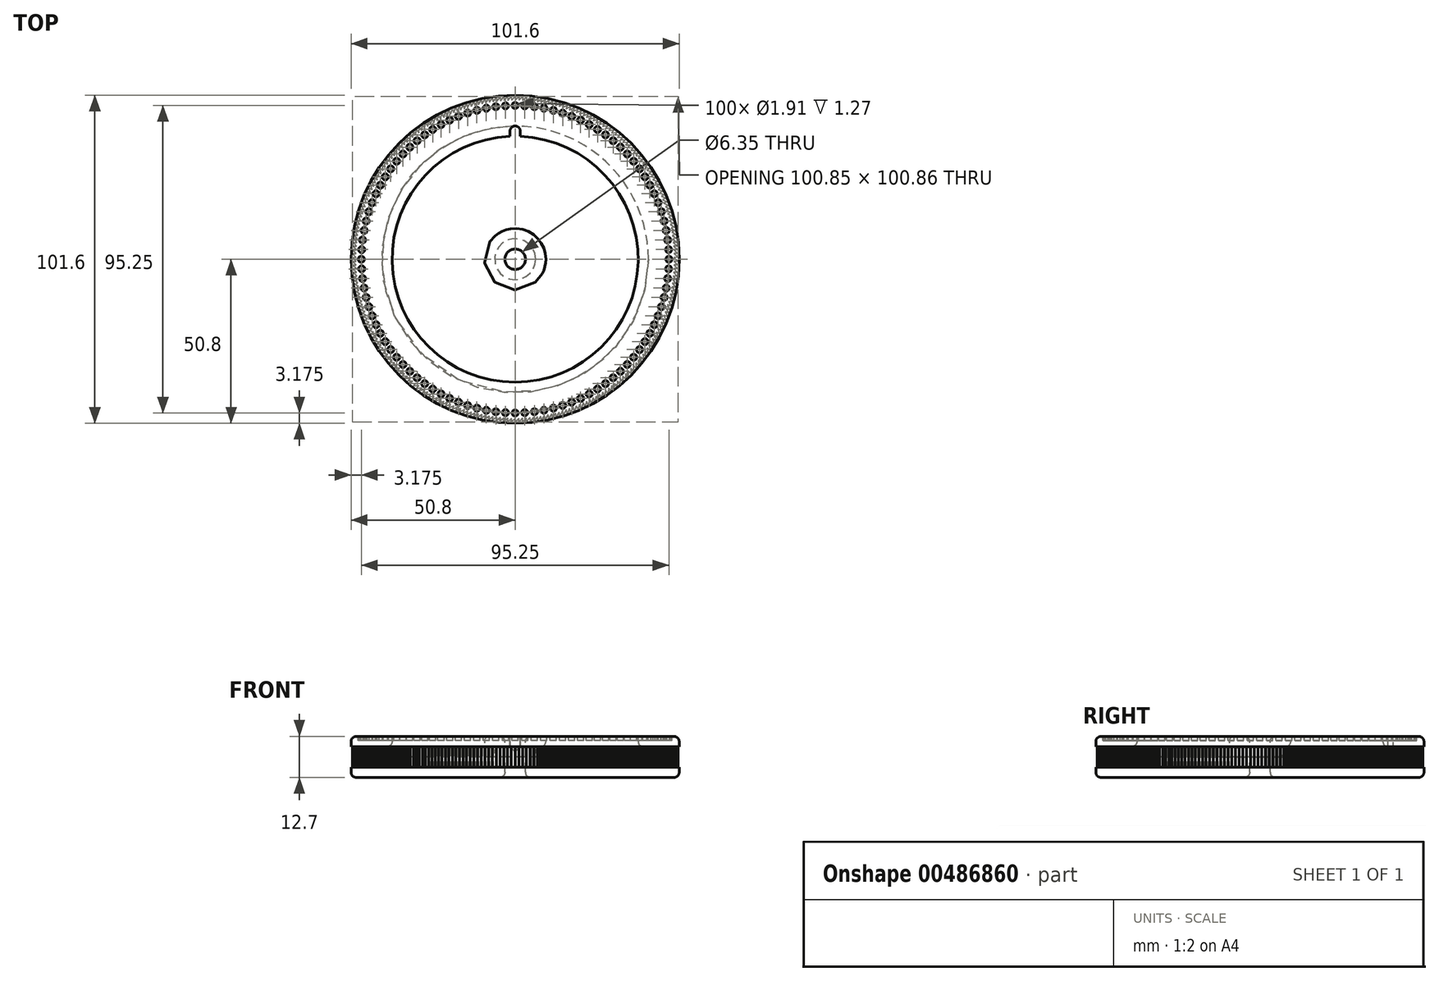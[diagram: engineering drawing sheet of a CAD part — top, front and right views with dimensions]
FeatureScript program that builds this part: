
annotation { "Feature Type Name" : "Feature", "Feature Type Description" : "" }
export const myFeature = defineFeature(function(context is Context, id is Id, definition is map)
    precondition{}
    {
        {
            var Q0;
            Q0=qCreatedBy(makeId("Top.planeOp"),FACE);
            var sketch = newSketch(context, id + "F0", { "sketchPlane" : qUnion([Q0])});
            skCircle(sketch, "E0", {"center": v(0, 0) * mm, "radius": 50.8 * mm});
            skSolve(sketch);
        }
        {
            var Q0;
            Q0 = qSketchRegion(id + "F0", true);
            extrude(context, id + "F1", {"entities" : qUnion([Q0]), "depth" : 12.7 * mm});
        }
        {
            var Q0;
            Q0=makeQuery(id+"F1.opExtrude","CAP_FACE",FACE,{"disambiguationData":[OSD([sQuery(id+"F0.wireOp",EDGE,"E0")])],"isStart":false});
            var sketch = newSketch(context, id + "F2", { "sketchPlane" : qUnion([Q0])});
            skCircle(sketch, "E1", {"center": v(0, 0) * mm, "radius": 38.1 * mm});
            skLineSegment(sketch, "E2", {"start": v(0, 0) * mm, "end": v(-3.18, 37.97) * mm});
            skLineSegment(sketch, "E3", {"start": v(0, 0) * mm, "end": v(0, 38.1) * mm});
            skLineSegment(sketch, "E4.1.0", {"start": v(0, 0) * mm, "end": v(-29.1, 24.6) * mm});
            skLineSegment(sketch, "E4.1.1", {"start": v(0, 0) * mm, "end": v(-26.94, 26.94) * mm});
            skLineSegment(sketch, "E4.2.0", {"start": v(0, 0) * mm, "end": v(-37.97, -3.17) * mm});
            skLineSegment(sketch, "E4.2.1", {"start": v(0, 0) * mm, "end": v(-38.1, 0) * mm});
            skLineSegment(sketch, "E4.3.0", {"start": v(0, 0) * mm, "end": v(-24.6, -29.1) * mm});
            skLineSegment(sketch, "E4.3.1", {"start": v(0, 0) * mm, "end": v(-26.94, -26.94) * mm});
            skLineSegment(sketch, "E4.4.0", {"start": v(0, 0) * mm, "end": v(3.17, -37.97) * mm});
            skLineSegment(sketch, "E4.4.1", {"start": v(0, 0) * mm, "end": v(0, -38.1) * mm});
            skLineSegment(sketch, "E4.5.0", {"start": v(0, 0) * mm, "end": v(29.1, -24.6) * mm});
            skLineSegment(sketch, "E4.5.1", {"start": v(0, 0) * mm, "end": v(26.94, -26.94) * mm});
            skLineSegment(sketch, "E4.6.0", {"start": v(0, 0) * mm, "end": v(37.97, 3.17) * mm});
            skLineSegment(sketch, "E4.6.1", {"start": v(0, 0) * mm, "end": v(38.1, 0) * mm});
            skLineSegment(sketch, "E4.7.0", {"start": v(0, 0) * mm, "end": v(24.6, 29.1) * mm});
            skLineSegment(sketch, "E4.7.1", {"start": v(0, 0) * mm, "end": v(26.94, 26.94) * mm});
            skCircle(sketch, "E5", {"center": v(0, 0) * mm, "radius": 3.18 * mm});
            skSolve(sketch);
        }
        {
            var Q0;
            Q0 = qSketchRegion(id + "F2", true);
            var Q1;
            {var subQ1=sQuery(id+"F2.wireOp",EDGE,"E3");var subQ3=sQuery(id+"F2.wireOp",EDGE,"E5");var subQ4=makeQuery(id+"F2.imprint","INTERSECT",VERTEX,{"derivedFrom":[subQ1,subQ3]});Q1=makeQuery(id+"F2.imprint","IMPRINT",FACE,{"disambiguationData":[TD([[makeQuery(id+"F2.imprint","IMPRINT",EDGE,{"disambiguationData":[TD([[subQ4,1.0]])],"derivedFrom":subQ3}),1.0]])]});}
            var Q2;
            {var subQ1=sQuery(id+"F2.wireOp",EDGE,"E4.6.0");var subQ3=sQuery(id+"F2.wireOp",EDGE,"E5");var subQ4=makeQuery(id+"F2.imprint","INTERSECT",VERTEX,{"derivedFrom":[subQ1,subQ3]});Q2=makeQuery(id+"F2.imprint","IMPRINT",FACE,{"disambiguationData":[TD([[makeQuery(id+"F2.imprint","IMPRINT",EDGE,{"disambiguationData":[TD([[subQ4,-1.0]])],"derivedFrom":subQ3}),1.0]])]});}
            var Q3;
            {var subQ1=sQuery(id+"F2.wireOp",EDGE,"E4.2.0");var subQ3=sQuery(id+"F2.wireOp",EDGE,"E5");var subQ4=makeQuery(id+"F2.imprint","INTERSECT",VERTEX,{"derivedFrom":[subQ1,subQ3]});Q3=makeQuery(id+"F2.imprint","IMPRINT",FACE,{"disambiguationData":[TD([[makeQuery(id+"F2.imprint","IMPRINT",EDGE,{"disambiguationData":[TD([[subQ4,-1.0]])],"derivedFrom":subQ3}),1.0]])]});}
            var Q4;
            {var subQ1=sQuery(id+"F2.wireOp",EDGE,"E4.1.0");var subQ3=sQuery(id+"F2.wireOp",EDGE,"E5");var subQ4=makeQuery(id+"F2.imprint","INTERSECT",VERTEX,{"derivedFrom":[subQ1,subQ3]});Q4=makeQuery(id+"F2.imprint","IMPRINT",FACE,{"disambiguationData":[TD([[makeQuery(id+"F2.imprint","IMPRINT",EDGE,{"disambiguationData":[TD([[subQ4,-1.0]])],"derivedFrom":subQ3}),1.0]])]});}
            var Q5;
            {var subQ1=sQuery(id+"F2.wireOp",EDGE,"E4.3.0");var subQ3=sQuery(id+"F2.wireOp",EDGE,"E5");var subQ4=makeQuery(id+"F2.imprint","INTERSECT",VERTEX,{"derivedFrom":[subQ1,subQ3]});Q5=makeQuery(id+"F2.imprint","IMPRINT",FACE,{"disambiguationData":[TD([[makeQuery(id+"F2.imprint","IMPRINT",EDGE,{"disambiguationData":[TD([[subQ4,-1.0]])],"derivedFrom":subQ3}),1.0]])]});}
            var Q6;
            {var subQ1=sQuery(id+"F2.wireOp",EDGE,"E4.4.0");var subQ3=sQuery(id+"F2.wireOp",EDGE,"E5");var subQ4=makeQuery(id+"F2.imprint","INTERSECT",VERTEX,{"derivedFrom":[subQ1,subQ3]});Q6=makeQuery(id+"F2.imprint","IMPRINT",FACE,{"disambiguationData":[TD([[makeQuery(id+"F2.imprint","IMPRINT",EDGE,{"disambiguationData":[TD([[subQ4,-1.0]])],"derivedFrom":subQ3}),1.0]])]});}
            var Q7;
            {var subQ1=sQuery(id+"F2.wireOp",EDGE,"E4.5.0");var subQ3=sQuery(id+"F2.wireOp",EDGE,"E5");var subQ4=makeQuery(id+"F2.imprint","INTERSECT",VERTEX,{"derivedFrom":[subQ1,subQ3]});Q7=makeQuery(id+"F2.imprint","IMPRINT",FACE,{"disambiguationData":[TD([[makeQuery(id+"F2.imprint","IMPRINT",EDGE,{"disambiguationData":[TD([[subQ4,-1.0]])],"derivedFrom":subQ3}),1.0]])]});}
            var Q8;
            {var subQ1=sQuery(id+"F2.wireOp",EDGE,"E2");var subQ3=sQuery(id+"F2.wireOp",EDGE,"E5");var subQ4=makeQuery(id+"F2.imprint","INTERSECT",VERTEX,{"derivedFrom":[subQ1,subQ3]});Q8=makeQuery(id+"F2.imprint","IMPRINT",FACE,{"disambiguationData":[TD([[makeQuery(id+"F2.imprint","IMPRINT",EDGE,{"disambiguationData":[TD([[subQ4,1.0]])],"derivedFrom":subQ3}),1.0]])]});}
            var Q9;
            {var subQ1=sQuery(id+"F2.wireOp",EDGE,"E2");var subQ3=sQuery(id+"F2.wireOp",EDGE,"E5");var subQ4=makeQuery(id+"F2.imprint","INTERSECT",VERTEX,{"derivedFrom":[subQ1,subQ3]});Q9=makeQuery(id+"F2.imprint","IMPRINT",FACE,{"disambiguationData":[TD([[makeQuery(id+"F2.imprint","IMPRINT",EDGE,{"disambiguationData":[TD([[subQ4,-1.0]])],"derivedFrom":subQ3}),1.0]])]});}
            var Q10;
            {var subQ1=sQuery(id+"F2.wireOp",EDGE,"E4.1.0");var subQ3=sQuery(id+"F2.wireOp",EDGE,"E5");var subQ4=makeQuery(id+"F2.imprint","INTERSECT",VERTEX,{"derivedFrom":[subQ1,subQ3]});Q10=makeQuery(id+"F2.imprint","IMPRINT",FACE,{"disambiguationData":[TD([[makeQuery(id+"F2.imprint","IMPRINT",EDGE,{"disambiguationData":[TD([[subQ4,1.0]])],"derivedFrom":subQ3}),1.0]])]});}
            var Q11;
            {var subQ1=sQuery(id+"F2.wireOp",EDGE,"E4.2.0");var subQ3=sQuery(id+"F2.wireOp",EDGE,"E5");var subQ4=makeQuery(id+"F2.imprint","INTERSECT",VERTEX,{"derivedFrom":[subQ1,subQ3]});Q11=makeQuery(id+"F2.imprint","IMPRINT",FACE,{"disambiguationData":[TD([[makeQuery(id+"F2.imprint","IMPRINT",EDGE,{"disambiguationData":[TD([[subQ4,1.0]])],"derivedFrom":subQ3}),1.0]])]});}
            var Q12;
            {var subQ1=sQuery(id+"F2.wireOp",EDGE,"E4.7.0");var subQ3=sQuery(id+"F2.wireOp",EDGE,"E5");var subQ4=makeQuery(id+"F2.imprint","INTERSECT",VERTEX,{"derivedFrom":[subQ1,subQ3]});Q12=makeQuery(id+"F2.imprint","IMPRINT",FACE,{"disambiguationData":[TD([[makeQuery(id+"F2.imprint","IMPRINT",EDGE,{"disambiguationData":[TD([[subQ4,1.0]])],"derivedFrom":subQ3}),1.0]])]});}
            var Q13;
            {var subQ1=sQuery(id+"F2.wireOp",EDGE,"E4.3.0");var subQ3=sQuery(id+"F2.wireOp",EDGE,"E5");var subQ4=makeQuery(id+"F2.imprint","INTERSECT",VERTEX,{"derivedFrom":[subQ1,subQ3]});Q13=makeQuery(id+"F2.imprint","IMPRINT",FACE,{"disambiguationData":[TD([[makeQuery(id+"F2.imprint","IMPRINT",EDGE,{"disambiguationData":[TD([[subQ4,1.0]])],"derivedFrom":subQ3}),1.0]])]});}
            var Q14;
            {var subQ1=sQuery(id+"F2.wireOp",EDGE,"E4.4.0");var subQ3=sQuery(id+"F2.wireOp",EDGE,"E5");var subQ4=makeQuery(id+"F2.imprint","INTERSECT",VERTEX,{"derivedFrom":[subQ1,subQ3]});Q14=makeQuery(id+"F2.imprint","IMPRINT",FACE,{"disambiguationData":[TD([[makeQuery(id+"F2.imprint","IMPRINT",EDGE,{"disambiguationData":[TD([[subQ4,1.0]])],"derivedFrom":subQ3}),1.0]])]});}
            var Q15;
            {var subQ1=sQuery(id+"F2.wireOp",EDGE,"E4.5.0");var subQ3=sQuery(id+"F2.wireOp",EDGE,"E5");var subQ4=makeQuery(id+"F2.imprint","INTERSECT",VERTEX,{"derivedFrom":[subQ1,subQ3]});Q15=makeQuery(id+"F2.imprint","IMPRINT",FACE,{"disambiguationData":[TD([[makeQuery(id+"F2.imprint","IMPRINT",EDGE,{"disambiguationData":[TD([[subQ4,1.0]])],"derivedFrom":subQ3}),1.0]])]});}
            var Q16;
            {var subQ1=sQuery(id+"F2.wireOp",EDGE,"E4.6.0");var subQ3=sQuery(id+"F2.wireOp",EDGE,"E5");var subQ4=makeQuery(id+"F2.imprint","INTERSECT",VERTEX,{"derivedFrom":[subQ1,subQ3]});Q16=makeQuery(id+"F2.imprint","IMPRINT",FACE,{"disambiguationData":[TD([[makeQuery(id+"F2.imprint","IMPRINT",EDGE,{"disambiguationData":[TD([[subQ4,1.0]])],"derivedFrom":subQ3}),1.0]])]});}
            extrude(context, id + "F3", {"entities" : qUnion([Q0, Q1, Q2, Q3, Q4, Q5, Q6, Q7, Q8, Q9, Q10, Q11, Q12, Q13, Q14, Q15, Q16]), "operationType" : NewBodyOperationType.REMOVE, "oppositeDirection" : true, "depth" : 6.35 * mm});
        }
        {
            var Q0;
            Q0=makeQuery(id+"F3.boolean.opBoolean","COPY",FACE,{"derivedFrom":makeQuery(id+"F3.opExtrude","CAP_FACE",FACE,{"disambiguationData":[OSD([sQuery(id+"F2.wireOp",EDGE,"E1")])],"isStart":false})});
            var sketch = newSketch(context, id + "F4", { "sketchPlane" : qUnion([Q0])});
            skCircle(sketch, "E6", {"center": v(0, 0) * mm, "radius": 3.18 * mm});
            skSolve(sketch);
        }
        {
            var Q0;
            Q0 = qSketchRegion(id + "F4", true);
            extrude(context, id + "F5", {"entities" : qUnion([Q0]), "operationType" : NewBodyOperationType.REMOVE, "oppositeDirection" : true, "depth" : 25.4 * mm});
        }
        {
            var Q0;
            Q0=qCreatedBy(makeId("Top.planeOp"),FACE);
            var sketch = newSketch(context, id + "F6", { "sketchPlane" : qUnion([Q0])});
            skLineSegment(sketch, "E7", {"start": v(0, 51.65) * mm, "end": v(0, 49.24) * mm});
            skLineSegment(sketch, "E8", {"start": v(0, 49.24) * mm, "end": v(2.41, 51.65) * mm});
            skLineSegment(sketch, "E9", {"start": v(2.41, 51.65) * mm, "end": v(0, 51.65) * mm});
            skLineSegment(sketch, "E10.1.0", {"start": v(-1.2, 51.64) * mm, "end": v(-1.15, 49.23) * mm});
            skLineSegment(sketch, "E10.1.1", {"start": v(1.2, 51.7) * mm, "end": v(-1.2, 51.64) * mm});
            skLineSegment(sketch, "E10.1.2", {"start": v(-1.15, 49.23) * mm, "end": v(1.2, 51.7) * mm});
            skLineSegment(sketch, "E10.2.0", {"start": v(-2.4, 51.6) * mm, "end": v(-2.3, 49.19) * mm});
            skLineSegment(sketch, "E10.2.1", {"start": v(0, 51.7) * mm, "end": v(-2.4, 51.6) * mm});
            skLineSegment(sketch, "E10.2.2", {"start": v(-2.3, 49.19) * mm, "end": v(0, 51.7) * mm});
            skLineSegment(sketch, "E10.3.0", {"start": v(-3.6, 51.53) * mm, "end": v(-3.43, 49.12) * mm});
            skLineSegment(sketch, "E10.3.1", {"start": v(-1.2, 51.7) * mm, "end": v(-3.6, 51.53) * mm});
            skLineSegment(sketch, "E10.3.2", {"start": v(-3.43, 49.12) * mm, "end": v(-1.2, 51.7) * mm});
            skLineSegment(sketch, "E10.4.0", {"start": v(-4.8, 51.43) * mm, "end": v(-4.58, 49.03) * mm});
            skLineSegment(sketch, "E10.4.1", {"start": v(-2.4, 51.65) * mm, "end": v(-4.8, 51.43) * mm});
            skLineSegment(sketch, "E10.4.2", {"start": v(-4.58, 49.03) * mm, "end": v(-2.4, 51.65) * mm});
            skLineSegment(sketch, "E10.5.0", {"start": v(-6, 51.3) * mm, "end": v(-5.72, 48.9) * mm});
            skLineSegment(sketch, "E10.5.1", {"start": v(-3.6, 51.58) * mm, "end": v(-6, 51.3) * mm});
            skLineSegment(sketch, "E10.5.2", {"start": v(-5.72, 48.9) * mm, "end": v(-3.6, 51.58) * mm});
            skLineSegment(sketch, "E10.6.0", {"start": v(-7.19, 51.15) * mm, "end": v(-6.85, 48.76) * mm});
            skLineSegment(sketch, "E10.6.1", {"start": v(-4.8, 51.49) * mm, "end": v(-7.19, 51.15) * mm});
            skLineSegment(sketch, "E10.6.2", {"start": v(-6.85, 48.76) * mm, "end": v(-4.8, 51.49) * mm});
            skLineSegment(sketch, "E10.7.0", {"start": v(-8.38, 50.97) * mm, "end": v(-7.99, 48.59) * mm});
            skLineSegment(sketch, "E10.7.1", {"start": v(-6, 51.36) * mm, "end": v(-8.38, 50.97) * mm});
            skLineSegment(sketch, "E10.7.2", {"start": v(-7.99, 48.59) * mm, "end": v(-6, 51.36) * mm});
            skLineSegment(sketch, "E10.8.0", {"start": v(-9.56, 50.76) * mm, "end": v(-9.11, 48.39) * mm});
            skLineSegment(sketch, "E10.8.1", {"start": v(-7.19, 51.2) * mm, "end": v(-9.56, 50.76) * mm});
            skLineSegment(sketch, "E10.8.2", {"start": v(-9.11, 48.39) * mm, "end": v(-7.19, 51.2) * mm});
            skLineSegment(sketch, "E10.9.0", {"start": v(-10.74, 50.52) * mm, "end": v(-10.24, 48.16) * mm});
            skLineSegment(sketch, "E10.9.1", {"start": v(-8.38, 51.03) * mm, "end": v(-10.74, 50.52) * mm});
            skLineSegment(sketch, "E10.9.2", {"start": v(-10.24, 48.16) * mm, "end": v(-8.38, 51.03) * mm});
            skLineSegment(sketch, "E10.10.0", {"start": v(-11.91, 50.26) * mm, "end": v(-11.36, 47.91) * mm});
            skLineSegment(sketch, "E10.10.1", {"start": v(-9.56, 50.82) * mm, "end": v(-11.91, 50.26) * mm});
            skLineSegment(sketch, "E10.10.2", {"start": v(-11.36, 47.91) * mm, "end": v(-9.56, 50.82) * mm});
            skLineSegment(sketch, "E10.11.0", {"start": v(-13.08, 49.97) * mm, "end": v(-12.47, 47.64) * mm});
            skLineSegment(sketch, "E10.11.1", {"start": v(-10.74, 50.58) * mm, "end": v(-13.08, 49.97) * mm});
            skLineSegment(sketch, "E10.11.2", {"start": v(-12.47, 47.64) * mm, "end": v(-10.74, 50.58) * mm});
            skLineSegment(sketch, "E10.12.0", {"start": v(-14.24, 49.65) * mm, "end": v(-13.57, 47.33) * mm});
            skLineSegment(sketch, "E10.12.1", {"start": v(-11.92, 50.32) * mm, "end": v(-14.24, 49.65) * mm});
            skLineSegment(sketch, "E10.12.2", {"start": v(-13.57, 47.33) * mm, "end": v(-11.92, 50.32) * mm});
            skLineSegment(sketch, "E10.13.0", {"start": v(-15.39, 49.3) * mm, "end": v(-14.67, 47) * mm});
            skLineSegment(sketch, "E10.13.1", {"start": v(-13.09, 50.03) * mm, "end": v(-15.39, 49.3) * mm});
            skLineSegment(sketch, "E10.13.2", {"start": v(-14.67, 47) * mm, "end": v(-13.09, 50.03) * mm});
            skLineSegment(sketch, "E10.14.0", {"start": v(-16.53, 48.94) * mm, "end": v(-15.76, 46.65) * mm});
            skLineSegment(sketch, "E10.14.1", {"start": v(-14.25, 49.7) * mm, "end": v(-16.53, 48.94) * mm});
            skLineSegment(sketch, "E10.14.2", {"start": v(-15.76, 46.65) * mm, "end": v(-14.25, 49.7) * mm});
            skLineSegment(sketch, "E10.15.0", {"start": v(-17.67, 48.54) * mm, "end": v(-16.84, 46.27) * mm});
            skLineSegment(sketch, "E10.15.1", {"start": v(-15.4, 49.36) * mm, "end": v(-17.67, 48.54) * mm});
            skLineSegment(sketch, "E10.15.2", {"start": v(-16.84, 46.27) * mm, "end": v(-15.4, 49.36) * mm});
            skLineSegment(sketch, "E10.16.0", {"start": v(-18.8, 48.11) * mm, "end": v(-17.91, 45.87) * mm});
            skLineSegment(sketch, "E10.16.1", {"start": v(-16.54, 49) * mm, "end": v(-18.8, 48.11) * mm});
            skLineSegment(sketch, "E10.16.2", {"start": v(-17.91, 45.87) * mm, "end": v(-16.54, 49) * mm});
            skLineSegment(sketch, "E10.17.0", {"start": v(-19.9, 47.66) * mm, "end": v(-18.98, 45.44) * mm});
            skLineSegment(sketch, "E10.17.1", {"start": v(-17.68, 48.6) * mm, "end": v(-19.9, 47.66) * mm});
            skLineSegment(sketch, "E10.17.2", {"start": v(-18.98, 45.44) * mm, "end": v(-17.68, 48.6) * mm});
            skLineSegment(sketch, "E10.18.0", {"start": v(-21, 47.19) * mm, "end": v(-20.03, 44.98) * mm});
            skLineSegment(sketch, "E10.18.1", {"start": v(-18.8, 48.17) * mm, "end": v(-21, 47.19) * mm});
            skLineSegment(sketch, "E10.18.2", {"start": v(-20.03, 44.98) * mm, "end": v(-18.8, 48.17) * mm});
            skLineSegment(sketch, "E10.19.0", {"start": v(-22.1, 46.69) * mm, "end": v(-21.07, 44.5) * mm});
            skLineSegment(sketch, "E10.19.1", {"start": v(-19.92, 47.72) * mm, "end": v(-22.1, 46.69) * mm});
            skLineSegment(sketch, "E10.19.2", {"start": v(-21.07, 44.5) * mm, "end": v(-19.92, 47.72) * mm});
            skLineSegment(sketch, "E10.20.0", {"start": v(-23.18, 46.16) * mm, "end": v(-22.1, 44) * mm});
            skLineSegment(sketch, "E10.20.1", {"start": v(-21.03, 47.24) * mm, "end": v(-23.18, 46.16) * mm});
            skLineSegment(sketch, "E10.20.2", {"start": v(-22.1, 44) * mm, "end": v(-21.03, 47.24) * mm});
            skLineSegment(sketch, "E10.21.0", {"start": v(-24.25, 45.6) * mm, "end": v(-23.12, 43.48) * mm});
            skLineSegment(sketch, "E10.21.1", {"start": v(-22.12, 46.74) * mm, "end": v(-24.25, 45.6) * mm});
            skLineSegment(sketch, "E10.21.2", {"start": v(-23.12, 43.48) * mm, "end": v(-22.12, 46.74) * mm});
            skLineSegment(sketch, "E10.22.0", {"start": v(-25.3, 45.03) * mm, "end": v(-24.12, 42.93) * mm});
            skLineSegment(sketch, "E10.22.1", {"start": v(-23.2, 46.21) * mm, "end": v(-25.3, 45.03) * mm});
            skLineSegment(sketch, "E10.22.2", {"start": v(-24.12, 42.93) * mm, "end": v(-23.2, 46.21) * mm});
            skLineSegment(sketch, "E10.23.0", {"start": v(-26.35, 44.43) * mm, "end": v(-25.11, 42.35) * mm});
            skLineSegment(sketch, "E10.23.1", {"start": v(-24.27, 45.66) * mm, "end": v(-26.35, 44.43) * mm});
            skLineSegment(sketch, "E10.23.2", {"start": v(-25.11, 42.35) * mm, "end": v(-24.27, 45.66) * mm});
            skLineSegment(sketch, "E10.24.0", {"start": v(-27.37, 43.8) * mm, "end": v(-26.1, 41.76) * mm});
            skLineSegment(sketch, "E10.24.1", {"start": v(-25.33, 45.08) * mm, "end": v(-27.37, 43.8) * mm});
            skLineSegment(sketch, "E10.24.2", {"start": v(-26.1, 41.76) * mm, "end": v(-25.33, 45.08) * mm});
            skLineSegment(sketch, "E10.25.0", {"start": v(-28.38, 43.16) * mm, "end": v(-27.06, 41.14) * mm});
            skLineSegment(sketch, "E10.25.1", {"start": v(-26.37, 44.48) * mm, "end": v(-28.38, 43.16) * mm});
            skLineSegment(sketch, "E10.25.2", {"start": v(-27.06, 41.14) * mm, "end": v(-26.37, 44.48) * mm});
            skLineSegment(sketch, "E10.26.0", {"start": v(-29.38, 42.48) * mm, "end": v(-28, 40.5) * mm});
            skLineSegment(sketch, "E10.26.1", {"start": v(-27.4, 43.86) * mm, "end": v(-29.38, 42.48) * mm});
            skLineSegment(sketch, "E10.26.2", {"start": v(-28, 40.5) * mm, "end": v(-27.4, 43.86) * mm});
            skLineSegment(sketch, "E10.27.0", {"start": v(-30.36, 41.79) * mm, "end": v(-28.94, 39.84) * mm});
            skLineSegment(sketch, "E10.27.1", {"start": v(-28.4, 43.2) * mm, "end": v(-30.36, 41.79) * mm});
            skLineSegment(sketch, "E10.27.2", {"start": v(-28.94, 39.84) * mm, "end": v(-28.4, 43.2) * mm});
            skLineSegment(sketch, "E10.28.0", {"start": v(-31.33, 41.07) * mm, "end": v(-29.86, 39.15) * mm});
            skLineSegment(sketch, "E10.28.1", {"start": v(-29.4, 42.53) * mm, "end": v(-31.33, 41.07) * mm});
            skLineSegment(sketch, "E10.28.2", {"start": v(-29.86, 39.15) * mm, "end": v(-29.4, 42.53) * mm});
            skLineSegment(sketch, "E10.29.0", {"start": v(-32.27, 40.33) * mm, "end": v(-30.77, 38.45) * mm});
            skLineSegment(sketch, "E10.29.1", {"start": v(-30.39, 41.84) * mm, "end": v(-32.27, 40.33) * mm});
            skLineSegment(sketch, "E10.29.2", {"start": v(-30.77, 38.45) * mm, "end": v(-30.39, 41.84) * mm});
            skLineSegment(sketch, "E10.30.0", {"start": v(-33.2, 39.57) * mm, "end": v(-31.65, 37.72) * mm});
            skLineSegment(sketch, "E10.30.1", {"start": v(-31.35, 41.12) * mm, "end": v(-33.2, 39.57) * mm});
            skLineSegment(sketch, "E10.30.2", {"start": v(-31.65, 37.72) * mm, "end": v(-31.35, 41.12) * mm});
            skLineSegment(sketch, "E10.31.0", {"start": v(-34.11, 38.79) * mm, "end": v(-32.52, 36.97) * mm});
            skLineSegment(sketch, "E10.31.1", {"start": v(-32.3, 40.38) * mm, "end": v(-34.11, 38.79) * mm});
            skLineSegment(sketch, "E10.31.2", {"start": v(-32.52, 36.97) * mm, "end": v(-32.3, 40.38) * mm});
            skLineSegment(sketch, "E10.32.0", {"start": v(-35, 37.98) * mm, "end": v(-33.37, 36.2) * mm});
            skLineSegment(sketch, "E10.32.1", {"start": v(-33.23, 39.62) * mm, "end": v(-35, 37.98) * mm});
            skLineSegment(sketch, "E10.32.2", {"start": v(-33.37, 36.2) * mm, "end": v(-33.23, 39.62) * mm});
            skLineSegment(sketch, "E10.33.0", {"start": v(-35.88, 37.16) * mm, "end": v(-34.2, 35.42) * mm});
            skLineSegment(sketch, "E10.33.1", {"start": v(-34.15, 38.83) * mm, "end": v(-35.88, 37.16) * mm});
            skLineSegment(sketch, "E10.33.2", {"start": v(-34.2, 35.42) * mm, "end": v(-34.15, 38.83) * mm});
            skLineSegment(sketch, "E10.34.0", {"start": v(-36.74, 36.31) * mm, "end": v(-35.02, 34.62) * mm});
            skLineSegment(sketch, "E10.34.1", {"start": v(-35.04, 38.03) * mm, "end": v(-36.74, 36.31) * mm});
            skLineSegment(sketch, "E10.34.2", {"start": v(-35.02, 34.62) * mm, "end": v(-35.04, 38.03) * mm});
            skLineSegment(sketch, "E10.35.0", {"start": v(-37.57, 35.45) * mm, "end": v(-35.82, 33.8) * mm});
            skLineSegment(sketch, "E10.35.1", {"start": v(-35.92, 37.2) * mm, "end": v(-37.57, 35.45) * mm});
            skLineSegment(sketch, "E10.35.2", {"start": v(-35.82, 33.8) * mm, "end": v(-35.92, 37.2) * mm});
            skLineSegment(sketch, "E10.36.0", {"start": v(-38.39, 34.56) * mm, "end": v(-36.6, 32.95) * mm});
            skLineSegment(sketch, "E10.36.1", {"start": v(-36.77, 36.36) * mm, "end": v(-38.39, 34.56) * mm});
            skLineSegment(sketch, "E10.36.2", {"start": v(-36.6, 32.95) * mm, "end": v(-36.77, 36.36) * mm});
            skLineSegment(sketch, "E10.37.0", {"start": v(-39.18, 33.66) * mm, "end": v(-37.35, 32.09) * mm});
            skLineSegment(sketch, "E10.37.1", {"start": v(-37.6, 35.5) * mm, "end": v(-39.18, 33.66) * mm});
            skLineSegment(sketch, "E10.37.2", {"start": v(-37.35, 32.09) * mm, "end": v(-37.6, 35.5) * mm});
            skLineSegment(sketch, "E10.38.0", {"start": v(-39.95, 32.74) * mm, "end": v(-38.09, 31.21) * mm});
            skLineSegment(sketch, "E10.38.1", {"start": v(-38.42, 34.6) * mm, "end": v(-39.95, 32.74) * mm});
            skLineSegment(sketch, "E10.38.2", {"start": v(-38.09, 31.21) * mm, "end": v(-38.42, 34.6) * mm});
            skLineSegment(sketch, "E10.39.0", {"start": v(-40.7, 31.8) * mm, "end": v(-38.8, 30.32) * mm});
            skLineSegment(sketch, "E10.39.1", {"start": v(-39.22, 33.7) * mm, "end": v(-40.7, 31.8) * mm});
            skLineSegment(sketch, "E10.39.2", {"start": v(-38.8, 30.32) * mm, "end": v(-39.22, 33.7) * mm});
            skLineSegment(sketch, "E10.40.0", {"start": v(-41.43, 30.85) * mm, "end": v(-39.5, 29.4) * mm});
            skLineSegment(sketch, "E10.40.1", {"start": v(-40, 32.78) * mm, "end": v(-41.43, 30.85) * mm});
            skLineSegment(sketch, "E10.40.2", {"start": v(-39.5, 29.4) * mm, "end": v(-40, 32.78) * mm});
            skLineSegment(sketch, "E10.41.0", {"start": v(-42.14, 29.87) * mm, "end": v(-40.17, 28.48) * mm});
            skLineSegment(sketch, "E10.41.1", {"start": v(-40.74, 31.84) * mm, "end": v(-42.14, 29.87) * mm});
            skLineSegment(sketch, "E10.41.2", {"start": v(-40.17, 28.48) * mm, "end": v(-40.74, 31.84) * mm});
            skLineSegment(sketch, "E10.42.0", {"start": v(-42.82, 28.88) * mm, "end": v(-40.82, 27.54) * mm});
            skLineSegment(sketch, "E10.42.1", {"start": v(-41.47, 30.88) * mm, "end": v(-42.82, 28.88) * mm});
            skLineSegment(sketch, "E10.42.2", {"start": v(-40.82, 27.54) * mm, "end": v(-41.47, 30.88) * mm});
            skLineSegment(sketch, "E10.43.0", {"start": v(-43.48, 27.88) * mm, "end": v(-41.45, 26.58) * mm});
            skLineSegment(sketch, "E10.43.1", {"start": v(-42.18, 29.91) * mm, "end": v(-43.48, 27.88) * mm});
            skLineSegment(sketch, "E10.43.2", {"start": v(-41.45, 26.58) * mm, "end": v(-42.18, 29.91) * mm});
            skLineSegment(sketch, "E10.44.0", {"start": v(-44.12, 26.86) * mm, "end": v(-42.06, 25.6) * mm});
            skLineSegment(sketch, "E10.44.1", {"start": v(-42.87, 28.92) * mm, "end": v(-44.12, 26.86) * mm});
            skLineSegment(sketch, "E10.44.2", {"start": v(-42.06, 25.6) * mm, "end": v(-42.87, 28.92) * mm});
            skLineSegment(sketch, "E10.45.0", {"start": v(-44.73, 25.83) * mm, "end": v(-42.64, 24.62) * mm});
            skLineSegment(sketch, "E10.45.1", {"start": v(-43.53, 27.92) * mm, "end": v(-44.73, 25.83) * mm});
            skLineSegment(sketch, "E10.45.2", {"start": v(-42.64, 24.62) * mm, "end": v(-43.53, 27.92) * mm});
            skLineSegment(sketch, "E10.46.0", {"start": v(-45.32, 24.78) * mm, "end": v(-43.2, 23.62) * mm});
            skLineSegment(sketch, "E10.46.1", {"start": v(-44.16, 26.9) * mm, "end": v(-45.32, 24.78) * mm});
            skLineSegment(sketch, "E10.46.2", {"start": v(-43.2, 23.62) * mm, "end": v(-44.16, 26.9) * mm});
            skLineSegment(sketch, "E10.47.0", {"start": v(-45.89, 23.72) * mm, "end": v(-43.74, 22.6) * mm});
            skLineSegment(sketch, "E10.47.1", {"start": v(-44.78, 25.86) * mm, "end": v(-45.89, 23.72) * mm});
            skLineSegment(sketch, "E10.47.2", {"start": v(-43.74, 22.6) * mm, "end": v(-44.78, 25.86) * mm});
            skLineSegment(sketch, "E10.48.0", {"start": v(-46.43, 22.64) * mm, "end": v(-44.26, 21.59) * mm});
            skLineSegment(sketch, "E10.48.1", {"start": v(-45.37, 24.81) * mm, "end": v(-46.43, 22.64) * mm});
            skLineSegment(sketch, "E10.48.2", {"start": v(-44.26, 21.59) * mm, "end": v(-45.37, 24.81) * mm});
            skLineSegment(sketch, "E10.49.0", {"start": v(-46.94, 21.56) * mm, "end": v(-44.75, 20.55) * mm});
            skLineSegment(sketch, "E10.49.1", {"start": v(-45.93, 23.75) * mm, "end": v(-46.94, 21.56) * mm});
            skLineSegment(sketch, "E10.49.2", {"start": v(-44.75, 20.55) * mm, "end": v(-45.93, 23.75) * mm});
            skLineSegment(sketch, "E10.50.0", {"start": v(-47.43, 20.46) * mm, "end": v(-45.21, 19.5) * mm});
            skLineSegment(sketch, "E10.50.1", {"start": v(-46.47, 22.67) * mm, "end": v(-47.43, 20.46) * mm});
            skLineSegment(sketch, "E10.50.2", {"start": v(-45.21, 19.5) * mm, "end": v(-46.47, 22.67) * mm});
            skLineSegment(sketch, "E10.51.0", {"start": v(-47.9, 19.35) * mm, "end": v(-45.66, 18.45) * mm});
            skLineSegment(sketch, "E10.51.1", {"start": v(-46.99, 21.59) * mm, "end": v(-47.9, 19.35) * mm});
            skLineSegment(sketch, "E10.51.2", {"start": v(-45.66, 18.45) * mm, "end": v(-46.99, 21.59) * mm});
            skLineSegment(sketch, "E10.52.0", {"start": v(-48.33, 18.23) * mm, "end": v(-46.07, 17.38) * mm});
            skLineSegment(sketch, "E10.52.1", {"start": v(-47.48, 20.49) * mm, "end": v(-48.33, 18.23) * mm});
            skLineSegment(sketch, "E10.52.2", {"start": v(-46.07, 17.38) * mm, "end": v(-47.48, 20.49) * mm});
            skLineSegment(sketch, "E10.53.0", {"start": v(-48.74, 17.1) * mm, "end": v(-46.46, 16.3) * mm});
            skLineSegment(sketch, "E10.53.1", {"start": v(-47.94, 19.38) * mm, "end": v(-48.74, 17.1) * mm});
            skLineSegment(sketch, "E10.53.2", {"start": v(-46.46, 16.3) * mm, "end": v(-47.94, 19.38) * mm});
            skLineSegment(sketch, "E10.54.0", {"start": v(-49.13, 15.96) * mm, "end": v(-46.83, 15.22) * mm});
            skLineSegment(sketch, "E10.54.1", {"start": v(-48.38, 18.26) * mm, "end": v(-49.13, 15.96) * mm});
            skLineSegment(sketch, "E10.54.2", {"start": v(-46.83, 15.22) * mm, "end": v(-48.38, 18.26) * mm});
            skLineSegment(sketch, "E10.55.0", {"start": v(-49.48, 14.81) * mm, "end": v(-47.17, 14.12) * mm});
            skLineSegment(sketch, "E10.55.1", {"start": v(-48.8, 17.13) * mm, "end": v(-49.48, 14.81) * mm});
            skLineSegment(sketch, "E10.55.2", {"start": v(-47.17, 14.12) * mm, "end": v(-48.8, 17.13) * mm});
            skLineSegment(sketch, "E10.56.0", {"start": v(-49.81, 13.66) * mm, "end": v(-47.49, 13.02) * mm});
            skLineSegment(sketch, "E10.56.1", {"start": v(-49.18, 15.99) * mm, "end": v(-49.81, 13.66) * mm});
            skLineSegment(sketch, "E10.56.2", {"start": v(-47.49, 13.02) * mm, "end": v(-49.18, 15.99) * mm});
            skLineSegment(sketch, "E10.57.0", {"start": v(-50.12, 12.5) * mm, "end": v(-47.78, 11.91) * mm});
            skLineSegment(sketch, "E10.57.1", {"start": v(-49.54, 14.84) * mm, "end": v(-50.12, 12.5) * mm});
            skLineSegment(sketch, "E10.57.2", {"start": v(-47.78, 11.91) * mm, "end": v(-49.54, 14.84) * mm});
            skLineSegment(sketch, "E10.58.0", {"start": v(-50.4, 11.33) * mm, "end": v(-48.04, 10.8) * mm});
            skLineSegment(sketch, "E10.58.1", {"start": v(-49.87, 13.68) * mm, "end": v(-50.4, 11.33) * mm});
            skLineSegment(sketch, "E10.58.2", {"start": v(-48.04, 10.8) * mm, "end": v(-49.87, 13.68) * mm});
            skLineSegment(sketch, "E10.59.0", {"start": v(-50.65, 10.15) * mm, "end": v(-48.28, 9.68) * mm});
            skLineSegment(sketch, "E10.59.1", {"start": v(-50.17, 12.52) * mm, "end": v(-50.65, 10.15) * mm});
            skLineSegment(sketch, "E10.59.2", {"start": v(-48.28, 9.68) * mm, "end": v(-50.17, 12.52) * mm});
            skLineSegment(sketch, "E10.60.0", {"start": v(-50.87, 8.97) * mm, "end": v(-48.5, 8.55) * mm});
            skLineSegment(sketch, "E10.60.1", {"start": v(-50.45, 11.35) * mm, "end": v(-50.87, 8.97) * mm});
            skLineSegment(sketch, "E10.60.2", {"start": v(-48.5, 8.55) * mm, "end": v(-50.45, 11.35) * mm});
            skLineSegment(sketch, "E10.61.0", {"start": v(-51.06, 7.78) * mm, "end": v(-48.68, 7.42) * mm});
            skLineSegment(sketch, "E10.61.1", {"start": v(-50.7, 10.17) * mm, "end": v(-51.06, 7.78) * mm});
            skLineSegment(sketch, "E10.61.2", {"start": v(-48.68, 7.42) * mm, "end": v(-50.7, 10.17) * mm});
            skLineSegment(sketch, "E10.62.0", {"start": v(-51.23, 6.6) * mm, "end": v(-48.84, 6.29) * mm});
            skLineSegment(sketch, "E10.62.1", {"start": v(-50.92, 8.99) * mm, "end": v(-51.23, 6.6) * mm});
            skLineSegment(sketch, "E10.62.2", {"start": v(-48.84, 6.29) * mm, "end": v(-50.92, 8.99) * mm});
            skLineSegment(sketch, "E10.63.0", {"start": v(-51.37, 5.4) * mm, "end": v(-48.97, 5.15) * mm});
            skLineSegment(sketch, "E10.63.1", {"start": v(-51.12, 7.8) * mm, "end": v(-51.37, 5.4) * mm});
            skLineSegment(sketch, "E10.63.2", {"start": v(-48.97, 5.15) * mm, "end": v(-51.12, 7.8) * mm});
            skLineSegment(sketch, "E10.64.0", {"start": v(-51.48, 4.2) * mm, "end": v(-49.08, 4) * mm});
            skLineSegment(sketch, "E10.64.1", {"start": v(-51.29, 6.6) * mm, "end": v(-51.48, 4.2) * mm});
            skLineSegment(sketch, "E10.64.2", {"start": v(-49.08, 4) * mm, "end": v(-51.29, 6.6) * mm});
            skLineSegment(sketch, "E10.65.0", {"start": v(-51.57, 3) * mm, "end": v(-49.16, 2.86) * mm});
            skLineSegment(sketch, "E10.65.1", {"start": v(-51.43, 5.41) * mm, "end": v(-51.57, 3) * mm});
            skLineSegment(sketch, "E10.65.2", {"start": v(-49.16, 2.86) * mm, "end": v(-51.43, 5.41) * mm});
            skLineSegment(sketch, "E10.66.0", {"start": v(-51.62, 1.8) * mm, "end": v(-49.21, 1.72) * mm});
            skLineSegment(sketch, "E10.66.1", {"start": v(-51.54, 4.21) * mm, "end": v(-51.62, 1.8) * mm});
            skLineSegment(sketch, "E10.66.2", {"start": v(-49.21, 1.72) * mm, "end": v(-51.54, 4.21) * mm});
            skLineSegment(sketch, "E10.67.0", {"start": v(-51.65, 0.6) * mm, "end": v(-49.24, 0.57) * mm});
            skLineSegment(sketch, "E10.67.1", {"start": v(-51.62, 3.01) * mm, "end": v(-51.65, 0.6) * mm});
            skLineSegment(sketch, "E10.67.2", {"start": v(-49.24, 0.57) * mm, "end": v(-51.62, 3.01) * mm});
            skLineSegment(sketch, "E10.68.0", {"start": v(-51.65, -0.6) * mm, "end": v(-49.24, -0.57) * mm});
            skLineSegment(sketch, "E10.68.1", {"start": v(-51.68, 1.81) * mm, "end": v(-51.65, -0.6) * mm});
            skLineSegment(sketch, "E10.68.2", {"start": v(-49.24, -0.57) * mm, "end": v(-51.68, 1.81) * mm});
            skLineSegment(sketch, "E10.69.0", {"start": v(-51.62, -1.8) * mm, "end": v(-49.21, -1.72) * mm});
            skLineSegment(sketch, "E10.69.1", {"start": v(-51.7, 0.6) * mm, "end": v(-51.62, -1.8) * mm});
            skLineSegment(sketch, "E10.69.2", {"start": v(-49.21, -1.72) * mm, "end": v(-51.7, 0.6) * mm});
            skLineSegment(sketch, "E10.70.0", {"start": v(-51.57, -3) * mm, "end": v(-49.16, -2.86) * mm});
            skLineSegment(sketch, "E10.70.1", {"start": v(-51.7, -0.6) * mm, "end": v(-51.57, -3) * mm});
            skLineSegment(sketch, "E10.70.2", {"start": v(-49.16, -2.86) * mm, "end": v(-51.7, -0.6) * mm});
            skLineSegment(sketch, "E10.71.0", {"start": v(-51.48, -4.2) * mm, "end": v(-49.08, -4) * mm});
            skLineSegment(sketch, "E10.71.1", {"start": v(-51.68, -1.8) * mm, "end": v(-51.48, -4.2) * mm});
            skLineSegment(sketch, "E10.71.2", {"start": v(-49.08, -4) * mm, "end": v(-51.68, -1.8) * mm});
            skLineSegment(sketch, "E10.72.0", {"start": v(-51.37, -5.4) * mm, "end": v(-48.97, -5.15) * mm});
            skLineSegment(sketch, "E10.72.1", {"start": v(-51.62, -3) * mm, "end": v(-51.37, -5.4) * mm});
            skLineSegment(sketch, "E10.72.2", {"start": v(-48.97, -5.15) * mm, "end": v(-51.62, -3) * mm});
            skLineSegment(sketch, "E10.73.0", {"start": v(-51.23, -6.6) * mm, "end": v(-48.84, -6.29) * mm});
            skLineSegment(sketch, "E10.73.1", {"start": v(-51.54, -4.2) * mm, "end": v(-51.23, -6.6) * mm});
            skLineSegment(sketch, "E10.73.2", {"start": v(-48.84, -6.29) * mm, "end": v(-51.54, -4.2) * mm});
            skLineSegment(sketch, "E10.74.0", {"start": v(-51.06, -7.78) * mm, "end": v(-48.68, -7.42) * mm});
            skLineSegment(sketch, "E10.74.1", {"start": v(-51.43, -5.4) * mm, "end": v(-51.06, -7.78) * mm});
            skLineSegment(sketch, "E10.74.2", {"start": v(-48.68, -7.42) * mm, "end": v(-51.43, -5.4) * mm});
            skLineSegment(sketch, "E10.75.0", {"start": v(-50.87, -8.97) * mm, "end": v(-48.5, -8.55) * mm});
            skLineSegment(sketch, "E10.75.1", {"start": v(-51.29, -6.6) * mm, "end": v(-50.87, -8.97) * mm});
            skLineSegment(sketch, "E10.75.2", {"start": v(-48.5, -8.55) * mm, "end": v(-51.29, -6.6) * mm});
            skLineSegment(sketch, "E10.76.0", {"start": v(-50.65, -10.15) * mm, "end": v(-48.28, -9.68) * mm});
            skLineSegment(sketch, "E10.76.1", {"start": v(-51.12, -7.79) * mm, "end": v(-50.65, -10.15) * mm});
            skLineSegment(sketch, "E10.76.2", {"start": v(-48.28, -9.68) * mm, "end": v(-51.12, -7.79) * mm});
            skLineSegment(sketch, "E10.77.0", {"start": v(-50.4, -11.33) * mm, "end": v(-48.04, -10.8) * mm});
            skLineSegment(sketch, "E10.77.1", {"start": v(-50.93, -8.97) * mm, "end": v(-50.4, -11.33) * mm});
            skLineSegment(sketch, "E10.77.2", {"start": v(-48.04, -10.8) * mm, "end": v(-50.93, -8.97) * mm});
            skLineSegment(sketch, "E10.78.0", {"start": v(-50.12, -12.5) * mm, "end": v(-47.78, -11.91) * mm});
            skLineSegment(sketch, "E10.78.1", {"start": v(-50.7, -10.16) * mm, "end": v(-50.12, -12.5) * mm});
            skLineSegment(sketch, "E10.78.2", {"start": v(-47.78, -11.91) * mm, "end": v(-50.7, -10.16) * mm});
            skLineSegment(sketch, "E10.79.0", {"start": v(-49.81, -13.66) * mm, "end": v(-47.49, -13.02) * mm});
            skLineSegment(sketch, "E10.79.1", {"start": v(-50.45, -11.33) * mm, "end": v(-49.81, -13.66) * mm});
            skLineSegment(sketch, "E10.79.2", {"start": v(-47.49, -13.02) * mm, "end": v(-50.45, -11.33) * mm});
            skLineSegment(sketch, "E10.80.0", {"start": v(-49.48, -14.81) * mm, "end": v(-47.17, -14.12) * mm});
            skLineSegment(sketch, "E10.80.1", {"start": v(-50.18, -12.5) * mm, "end": v(-49.48, -14.81) * mm});
            skLineSegment(sketch, "E10.80.2", {"start": v(-47.17, -14.12) * mm, "end": v(-50.18, -12.5) * mm});
            skLineSegment(sketch, "E10.81.0", {"start": v(-49.13, -15.96) * mm, "end": v(-46.83, -15.22) * mm});
            skLineSegment(sketch, "E10.81.1", {"start": v(-49.87, -13.67) * mm, "end": v(-49.13, -15.96) * mm});
            skLineSegment(sketch, "E10.81.2", {"start": v(-46.83, -15.22) * mm, "end": v(-49.87, -13.67) * mm});
            skLineSegment(sketch, "E10.82.0", {"start": v(-48.74, -17.1) * mm, "end": v(-46.46, -16.3) * mm});
            skLineSegment(sketch, "E10.82.1", {"start": v(-49.54, -14.82) * mm, "end": v(-48.74, -17.1) * mm});
            skLineSegment(sketch, "E10.82.2", {"start": v(-46.46, -16.3) * mm, "end": v(-49.54, -14.82) * mm});
            skLineSegment(sketch, "E10.83.0", {"start": v(-48.33, -18.23) * mm, "end": v(-46.07, -17.38) * mm});
            skLineSegment(sketch, "E10.83.1", {"start": v(-49.18, -15.97) * mm, "end": v(-48.33, -18.23) * mm});
            skLineSegment(sketch, "E10.83.2", {"start": v(-46.07, -17.38) * mm, "end": v(-49.18, -15.97) * mm});
            skLineSegment(sketch, "E10.84.0", {"start": v(-47.9, -19.35) * mm, "end": v(-45.66, -18.45) * mm});
            skLineSegment(sketch, "E10.84.1", {"start": v(-48.8, -17.11) * mm, "end": v(-47.9, -19.35) * mm});
            skLineSegment(sketch, "E10.84.2", {"start": v(-45.66, -18.45) * mm, "end": v(-48.8, -17.11) * mm});
            skLineSegment(sketch, "E10.85.0", {"start": v(-47.43, -20.46) * mm, "end": v(-45.21, -19.5) * mm});
            skLineSegment(sketch, "E10.85.1", {"start": v(-48.38, -18.24) * mm, "end": v(-47.43, -20.46) * mm});
            skLineSegment(sketch, "E10.85.2", {"start": v(-45.21, -19.5) * mm, "end": v(-48.38, -18.24) * mm});
            skLineSegment(sketch, "E10.86.0", {"start": v(-46.94, -21.56) * mm, "end": v(-44.75, -20.55) * mm});
            skLineSegment(sketch, "E10.86.1", {"start": v(-47.95, -19.36) * mm, "end": v(-46.94, -21.56) * mm});
            skLineSegment(sketch, "E10.86.2", {"start": v(-44.75, -20.55) * mm, "end": v(-47.95, -19.36) * mm});
            skLineSegment(sketch, "E10.87.0", {"start": v(-46.43, -22.64) * mm, "end": v(-44.26, -21.59) * mm});
            skLineSegment(sketch, "E10.87.1", {"start": v(-47.48, -20.48) * mm, "end": v(-46.43, -22.64) * mm});
            skLineSegment(sketch, "E10.87.2", {"start": v(-44.26, -21.59) * mm, "end": v(-47.48, -20.48) * mm});
            skLineSegment(sketch, "E10.88.0", {"start": v(-45.89, -23.72) * mm, "end": v(-43.74, -22.6) * mm});
            skLineSegment(sketch, "E10.88.1", {"start": v(-47, -21.57) * mm, "end": v(-45.89, -23.72) * mm});
            skLineSegment(sketch, "E10.88.2", {"start": v(-43.74, -22.6) * mm, "end": v(-47, -21.57) * mm});
            skLineSegment(sketch, "E10.89.0", {"start": v(-45.32, -24.78) * mm, "end": v(-43.2, -23.62) * mm});
            skLineSegment(sketch, "E10.89.1", {"start": v(-46.48, -22.66) * mm, "end": v(-45.32, -24.78) * mm});
            skLineSegment(sketch, "E10.89.2", {"start": v(-43.2, -23.62) * mm, "end": v(-46.48, -22.66) * mm});
            skLineSegment(sketch, "E10.90.0", {"start": v(-44.73, -25.83) * mm, "end": v(-42.64, -24.62) * mm});
            skLineSegment(sketch, "E10.90.1", {"start": v(-45.94, -23.74) * mm, "end": v(-44.73, -25.83) * mm});
            skLineSegment(sketch, "E10.90.2", {"start": v(-42.64, -24.62) * mm, "end": v(-45.94, -23.74) * mm});
            skLineSegment(sketch, "E10.91.0", {"start": v(-44.12, -26.86) * mm, "end": v(-42.06, -25.6) * mm});
            skLineSegment(sketch, "E10.91.1", {"start": v(-45.37, -24.8) * mm, "end": v(-44.12, -26.86) * mm});
            skLineSegment(sketch, "E10.91.2", {"start": v(-42.06, -25.6) * mm, "end": v(-45.37, -24.8) * mm});
            skLineSegment(sketch, "E10.92.0", {"start": v(-43.48, -27.88) * mm, "end": v(-41.45, -26.58) * mm});
            skLineSegment(sketch, "E10.92.1", {"start": v(-44.79, -25.85) * mm, "end": v(-43.48, -27.88) * mm});
            skLineSegment(sketch, "E10.92.2", {"start": v(-41.45, -26.58) * mm, "end": v(-44.79, -25.85) * mm});
            skLineSegment(sketch, "E10.93.0", {"start": v(-42.82, -28.88) * mm, "end": v(-40.82, -27.54) * mm});
            skLineSegment(sketch, "E10.93.1", {"start": v(-44.17, -26.88) * mm, "end": v(-42.82, -28.88) * mm});
            skLineSegment(sketch, "E10.93.2", {"start": v(-40.82, -27.54) * mm, "end": v(-44.17, -26.88) * mm});
            skLineSegment(sketch, "E10.94.0", {"start": v(-42.14, -29.87) * mm, "end": v(-40.17, -28.48) * mm});
            skLineSegment(sketch, "E10.94.1", {"start": v(-43.53, -27.9) * mm, "end": v(-42.14, -29.87) * mm});
            skLineSegment(sketch, "E10.94.2", {"start": v(-40.17, -28.48) * mm, "end": v(-43.53, -27.9) * mm});
            skLineSegment(sketch, "E10.95.0", {"start": v(-41.43, -30.85) * mm, "end": v(-39.5, -29.4) * mm});
            skLineSegment(sketch, "E10.95.1", {"start": v(-42.87, -28.91) * mm, "end": v(-41.43, -30.85) * mm});
            skLineSegment(sketch, "E10.95.2", {"start": v(-39.5, -29.4) * mm, "end": v(-42.87, -28.91) * mm});
            skLineSegment(sketch, "E10.96.0", {"start": v(-40.7, -31.8) * mm, "end": v(-38.8, -30.32) * mm});
            skLineSegment(sketch, "E10.96.1", {"start": v(-42.19, -29.9) * mm, "end": v(-40.7, -31.8) * mm});
            skLineSegment(sketch, "E10.96.2", {"start": v(-38.8, -30.32) * mm, "end": v(-42.19, -29.9) * mm});
            skLineSegment(sketch, "E10.97.0", {"start": v(-39.95, -32.74) * mm, "end": v(-38.09, -31.21) * mm});
            skLineSegment(sketch, "E10.97.1", {"start": v(-41.48, -30.87) * mm, "end": v(-39.95, -32.74) * mm});
            skLineSegment(sketch, "E10.97.2", {"start": v(-38.09, -31.21) * mm, "end": v(-41.48, -30.87) * mm});
            skLineSegment(sketch, "E10.98.0", {"start": v(-39.18, -33.66) * mm, "end": v(-37.35, -32.09) * mm});
            skLineSegment(sketch, "E10.98.1", {"start": v(-40.75, -31.83) * mm, "end": v(-39.18, -33.66) * mm});
            skLineSegment(sketch, "E10.98.2", {"start": v(-37.35, -32.09) * mm, "end": v(-40.75, -31.83) * mm});
            skLineSegment(sketch, "E10.99.0", {"start": v(-38.39, -34.56) * mm, "end": v(-36.6, -32.95) * mm});
            skLineSegment(sketch, "E10.99.1", {"start": v(-40, -32.77) * mm, "end": v(-38.39, -34.56) * mm});
            skLineSegment(sketch, "E10.99.2", {"start": v(-36.6, -32.95) * mm, "end": v(-40, -32.77) * mm});
            skLineSegment(sketch, "E10.100.0", {"start": v(-37.57, -35.45) * mm, "end": v(-35.82, -33.8) * mm});
            skLineSegment(sketch, "E10.100.1", {"start": v(-39.23, -33.7) * mm, "end": v(-37.57, -35.45) * mm});
            skLineSegment(sketch, "E10.100.2", {"start": v(-35.82, -33.8) * mm, "end": v(-39.23, -33.7) * mm});
            skLineSegment(sketch, "E10.101.0", {"start": v(-36.74, -36.31) * mm, "end": v(-35.02, -34.62) * mm});
            skLineSegment(sketch, "E10.101.1", {"start": v(-38.43, -34.6) * mm, "end": v(-36.74, -36.31) * mm});
            skLineSegment(sketch, "E10.101.2", {"start": v(-35.02, -34.62) * mm, "end": v(-38.43, -34.6) * mm});
            skLineSegment(sketch, "E10.102.0", {"start": v(-35.88, -37.16) * mm, "end": v(-34.2, -35.42) * mm});
            skLineSegment(sketch, "E10.102.1", {"start": v(-37.62, -35.48) * mm, "end": v(-35.88, -37.16) * mm});
            skLineSegment(sketch, "E10.102.2", {"start": v(-34.2, -35.42) * mm, "end": v(-37.62, -35.48) * mm});
            skLineSegment(sketch, "E10.103.0", {"start": v(-35, -37.98) * mm, "end": v(-33.37, -36.2) * mm});
            skLineSegment(sketch, "E10.103.1", {"start": v(-36.78, -36.35) * mm, "end": v(-35, -37.98) * mm});
            skLineSegment(sketch, "E10.103.2", {"start": v(-33.37, -36.2) * mm, "end": v(-36.78, -36.35) * mm});
            skLineSegment(sketch, "E10.104.0", {"start": v(-34.11, -38.79) * mm, "end": v(-32.52, -36.97) * mm});
            skLineSegment(sketch, "E10.104.1", {"start": v(-35.93, -37.2) * mm, "end": v(-34.11, -38.79) * mm});
            skLineSegment(sketch, "E10.104.2", {"start": v(-32.52, -36.97) * mm, "end": v(-35.93, -37.2) * mm});
            skLineSegment(sketch, "E10.105.0", {"start": v(-33.2, -39.57) * mm, "end": v(-31.65, -37.72) * mm});
            skLineSegment(sketch, "E10.105.1", {"start": v(-35.05, -38.02) * mm, "end": v(-33.2, -39.57) * mm});
            skLineSegment(sketch, "E10.105.2", {"start": v(-31.65, -37.72) * mm, "end": v(-35.05, -38.02) * mm});
            skLineSegment(sketch, "E10.106.0", {"start": v(-32.27, -40.33) * mm, "end": v(-30.77, -38.45) * mm});
            skLineSegment(sketch, "E10.106.1", {"start": v(-34.16, -38.82) * mm, "end": v(-32.27, -40.33) * mm});
            skLineSegment(sketch, "E10.106.2", {"start": v(-30.77, -38.45) * mm, "end": v(-34.16, -38.82) * mm});
            skLineSegment(sketch, "E10.107.0", {"start": v(-31.33, -41.07) * mm, "end": v(-29.86, -39.15) * mm});
            skLineSegment(sketch, "E10.107.1", {"start": v(-33.24, -39.6) * mm, "end": v(-31.33, -41.07) * mm});
            skLineSegment(sketch, "E10.107.2", {"start": v(-29.86, -39.15) * mm, "end": v(-33.24, -39.6) * mm});
            skLineSegment(sketch, "E10.108.0", {"start": v(-30.36, -41.79) * mm, "end": v(-28.94, -39.84) * mm});
            skLineSegment(sketch, "E10.108.1", {"start": v(-32.31, -40.37) * mm, "end": v(-30.36, -41.79) * mm});
            skLineSegment(sketch, "E10.108.2", {"start": v(-28.94, -39.84) * mm, "end": v(-32.31, -40.37) * mm});
            skLineSegment(sketch, "E10.109.0", {"start": v(-29.38, -42.48) * mm, "end": v(-28, -40.5) * mm});
            skLineSegment(sketch, "E10.109.1", {"start": v(-31.36, -41.11) * mm, "end": v(-29.38, -42.48) * mm});
            skLineSegment(sketch, "E10.109.2", {"start": v(-28, -40.5) * mm, "end": v(-31.36, -41.11) * mm});
            skLineSegment(sketch, "E10.110.0", {"start": v(-28.38, -43.16) * mm, "end": v(-27.06, -41.14) * mm});
            skLineSegment(sketch, "E10.110.1", {"start": v(-30.4, -41.83) * mm, "end": v(-28.38, -43.16) * mm});
            skLineSegment(sketch, "E10.110.2", {"start": v(-27.06, -41.14) * mm, "end": v(-30.4, -41.83) * mm});
            skLineSegment(sketch, "E10.111.0", {"start": v(-27.37, -43.8) * mm, "end": v(-26.1, -41.76) * mm});
            skLineSegment(sketch, "E10.111.1", {"start": v(-29.42, -42.53) * mm, "end": v(-27.37, -43.8) * mm});
            skLineSegment(sketch, "E10.111.2", {"start": v(-26.1, -41.76) * mm, "end": v(-29.42, -42.53) * mm});
            skLineSegment(sketch, "E10.112.0", {"start": v(-26.35, -44.43) * mm, "end": v(-25.11, -42.35) * mm});
            skLineSegment(sketch, "E10.112.1", {"start": v(-28.42, -43.2) * mm, "end": v(-26.35, -44.43) * mm});
            skLineSegment(sketch, "E10.112.2", {"start": v(-25.11, -42.35) * mm, "end": v(-28.42, -43.2) * mm});
            skLineSegment(sketch, "E10.113.0", {"start": v(-25.3, -45.03) * mm, "end": v(-24.12, -42.93) * mm});
            skLineSegment(sketch, "E10.113.1", {"start": v(-27.4, -43.85) * mm, "end": v(-25.3, -45.03) * mm});
            skLineSegment(sketch, "E10.113.2", {"start": v(-24.12, -42.93) * mm, "end": v(-27.4, -43.85) * mm});
            skLineSegment(sketch, "E10.114.0", {"start": v(-24.25, -45.6) * mm, "end": v(-23.12, -43.48) * mm});
            skLineSegment(sketch, "E10.114.1", {"start": v(-26.38, -44.47) * mm, "end": v(-24.25, -45.6) * mm});
            skLineSegment(sketch, "E10.114.2", {"start": v(-23.12, -43.48) * mm, "end": v(-26.38, -44.47) * mm});
            skLineSegment(sketch, "E10.115.0", {"start": v(-23.18, -46.16) * mm, "end": v(-22.1, -44) * mm});
            skLineSegment(sketch, "E10.115.1", {"start": v(-25.34, -45.08) * mm, "end": v(-23.18, -46.16) * mm});
            skLineSegment(sketch, "E10.115.2", {"start": v(-22.1, -44) * mm, "end": v(-25.34, -45.08) * mm});
            skLineSegment(sketch, "E10.116.0", {"start": v(-22.1, -46.69) * mm, "end": v(-21.07, -44.5) * mm});
            skLineSegment(sketch, "E10.116.1", {"start": v(-24.28, -45.65) * mm, "end": v(-22.1, -46.69) * mm});
            skLineSegment(sketch, "E10.116.2", {"start": v(-21.07, -44.5) * mm, "end": v(-24.28, -45.65) * mm});
            skLineSegment(sketch, "E10.117.0", {"start": v(-21, -47.19) * mm, "end": v(-20.03, -44.98) * mm});
            skLineSegment(sketch, "E10.117.1", {"start": v(-23.21, -46.2) * mm, "end": v(-21, -47.19) * mm});
            skLineSegment(sketch, "E10.117.2", {"start": v(-20.03, -44.98) * mm, "end": v(-23.21, -46.2) * mm});
            skLineSegment(sketch, "E10.118.0", {"start": v(-19.9, -47.66) * mm, "end": v(-18.98, -45.44) * mm});
            skLineSegment(sketch, "E10.118.1", {"start": v(-22.13, -46.73) * mm, "end": v(-19.9, -47.66) * mm});
            skLineSegment(sketch, "E10.118.2", {"start": v(-18.98, -45.44) * mm, "end": v(-22.13, -46.73) * mm});
            skLineSegment(sketch, "E10.119.0", {"start": v(-18.8, -48.11) * mm, "end": v(-17.91, -45.87) * mm});
            skLineSegment(sketch, "E10.119.1", {"start": v(-21.04, -47.24) * mm, "end": v(-18.8, -48.11) * mm});
            skLineSegment(sketch, "E10.119.2", {"start": v(-17.91, -45.87) * mm, "end": v(-21.04, -47.24) * mm});
            skLineSegment(sketch, "E10.120.0", {"start": v(-17.67, -48.54) * mm, "end": v(-16.84, -46.27) * mm});
            skLineSegment(sketch, "E10.120.1", {"start": v(-19.93, -47.71) * mm, "end": v(-17.67, -48.54) * mm});
            skLineSegment(sketch, "E10.120.2", {"start": v(-16.84, -46.27) * mm, "end": v(-19.93, -47.71) * mm});
            skLineSegment(sketch, "E10.121.0", {"start": v(-16.53, -48.94) * mm, "end": v(-15.76, -46.65) * mm});
            skLineSegment(sketch, "E10.121.1", {"start": v(-18.82, -48.16) * mm, "end": v(-16.53, -48.94) * mm});
            skLineSegment(sketch, "E10.121.2", {"start": v(-15.76, -46.65) * mm, "end": v(-18.82, -48.16) * mm});
            skLineSegment(sketch, "E10.122.0", {"start": v(-15.39, -49.3) * mm, "end": v(-14.67, -47) * mm});
            skLineSegment(sketch, "E10.122.1", {"start": v(-17.7, -48.59) * mm, "end": v(-15.39, -49.3) * mm});
            skLineSegment(sketch, "E10.122.2", {"start": v(-14.67, -47) * mm, "end": v(-17.7, -48.59) * mm});
            skLineSegment(sketch, "E10.123.0", {"start": v(-14.24, -49.65) * mm, "end": v(-13.57, -47.33) * mm});
            skLineSegment(sketch, "E10.123.1", {"start": v(-16.56, -48.99) * mm, "end": v(-14.24, -49.65) * mm});
            skLineSegment(sketch, "E10.123.2", {"start": v(-13.57, -47.33) * mm, "end": v(-16.56, -48.99) * mm});
            skLineSegment(sketch, "E10.124.0", {"start": v(-13.08, -49.97) * mm, "end": v(-12.47, -47.64) * mm});
            skLineSegment(sketch, "E10.124.1", {"start": v(-15.41, -49.36) * mm, "end": v(-13.08, -49.97) * mm});
            skLineSegment(sketch, "E10.124.2", {"start": v(-12.47, -47.64) * mm, "end": v(-15.41, -49.36) * mm});
            skLineSegment(sketch, "E10.125.0", {"start": v(-11.91, -50.26) * mm, "end": v(-11.36, -47.91) * mm});
            skLineSegment(sketch, "E10.125.1", {"start": v(-14.26, -49.7) * mm, "end": v(-11.91, -50.26) * mm});
            skLineSegment(sketch, "E10.125.2", {"start": v(-11.36, -47.91) * mm, "end": v(-14.26, -49.7) * mm});
            skLineSegment(sketch, "E10.126.0", {"start": v(-10.74, -50.52) * mm, "end": v(-10.24, -48.16) * mm});
            skLineSegment(sketch, "E10.126.1", {"start": v(-13.1, -50.02) * mm, "end": v(-10.74, -50.52) * mm});
            skLineSegment(sketch, "E10.126.2", {"start": v(-10.24, -48.16) * mm, "end": v(-13.1, -50.02) * mm});
            skLineSegment(sketch, "E10.127.0", {"start": v(-9.56, -50.76) * mm, "end": v(-9.11, -48.39) * mm});
            skLineSegment(sketch, "E10.127.1", {"start": v(-11.93, -50.31) * mm, "end": v(-9.56, -50.76) * mm});
            skLineSegment(sketch, "E10.127.2", {"start": v(-9.11, -48.39) * mm, "end": v(-11.93, -50.31) * mm});
            skLineSegment(sketch, "E10.128.0", {"start": v(-8.38, -50.97) * mm, "end": v(-7.99, -48.59) * mm});
            skLineSegment(sketch, "E10.128.1", {"start": v(-10.76, -50.58) * mm, "end": v(-8.38, -50.97) * mm});
            skLineSegment(sketch, "E10.128.2", {"start": v(-7.99, -48.59) * mm, "end": v(-10.76, -50.58) * mm});
            skLineSegment(sketch, "E10.129.0", {"start": v(-7.19, -51.15) * mm, "end": v(-6.85, -48.76) * mm});
            skLineSegment(sketch, "E10.129.1", {"start": v(-9.58, -50.81) * mm, "end": v(-7.19, -51.15) * mm});
            skLineSegment(sketch, "E10.129.2", {"start": v(-6.85, -48.76) * mm, "end": v(-9.58, -50.81) * mm});
            skLineSegment(sketch, "E10.130.0", {"start": v(-6, -51.3) * mm, "end": v(-5.72, -48.9) * mm});
            skLineSegment(sketch, "E10.130.1", {"start": v(-8.4, -51.02) * mm, "end": v(-6, -51.3) * mm});
            skLineSegment(sketch, "E10.130.2", {"start": v(-5.72, -48.9) * mm, "end": v(-8.4, -51.02) * mm});
            skLineSegment(sketch, "E10.131.0", {"start": v(-4.8, -51.43) * mm, "end": v(-4.58, -49.03) * mm});
            skLineSegment(sketch, "E10.131.1", {"start": v(-7.2, -51.2) * mm, "end": v(-4.8, -51.43) * mm});
            skLineSegment(sketch, "E10.131.2", {"start": v(-4.58, -49.03) * mm, "end": v(-7.2, -51.2) * mm});
            skLineSegment(sketch, "E10.132.0", {"start": v(-3.6, -51.53) * mm, "end": v(-3.43, -49.12) * mm});
            skLineSegment(sketch, "E10.132.1", {"start": v(-6, -51.36) * mm, "end": v(-3.6, -51.53) * mm});
            skLineSegment(sketch, "E10.132.2", {"start": v(-3.43, -49.12) * mm, "end": v(-6, -51.36) * mm});
            skLineSegment(sketch, "E10.133.0", {"start": v(-2.4, -51.6) * mm, "end": v(-2.3, -49.19) * mm});
            skLineSegment(sketch, "E10.133.1", {"start": v(-4.81, -51.49) * mm, "end": v(-2.4, -51.6) * mm});
            skLineSegment(sketch, "E10.133.2", {"start": v(-2.3, -49.19) * mm, "end": v(-4.81, -51.49) * mm});
            skLineSegment(sketch, "E10.134.0", {"start": v(-1.2, -51.64) * mm, "end": v(-1.15, -49.23) * mm});
            skLineSegment(sketch, "E10.134.1", {"start": v(-3.61, -51.58) * mm, "end": v(-1.2, -51.64) * mm});
            skLineSegment(sketch, "E10.134.2", {"start": v(-1.15, -49.23) * mm, "end": v(-3.61, -51.58) * mm});
            skLineSegment(sketch, "E10.135.0", {"start": v(0, -51.65) * mm, "end": v(0, -49.24) * mm});
            skLineSegment(sketch, "E10.135.1", {"start": v(-2.41, -51.65) * mm, "end": v(0, -51.65) * mm});
            skLineSegment(sketch, "E10.135.2", {"start": v(0, -49.24) * mm, "end": v(-2.41, -51.65) * mm});
            skLineSegment(sketch, "E10.136.0", {"start": v(1.2, -51.64) * mm, "end": v(1.15, -49.23) * mm});
            skLineSegment(sketch, "E10.136.1", {"start": v(-1.2, -51.7) * mm, "end": v(1.2, -51.64) * mm});
            skLineSegment(sketch, "E10.136.2", {"start": v(1.15, -49.23) * mm, "end": v(-1.2, -51.7) * mm});
            skLineSegment(sketch, "E10.137.0", {"start": v(2.4, -51.6) * mm, "end": v(2.3, -49.19) * mm});
            skLineSegment(sketch, "E10.137.1", {"start": v(0, -51.7) * mm, "end": v(2.4, -51.6) * mm});
            skLineSegment(sketch, "E10.137.2", {"start": v(2.3, -49.19) * mm, "end": v(0, -51.7) * mm});
            skLineSegment(sketch, "E10.138.0", {"start": v(3.6, -51.53) * mm, "end": v(3.43, -49.12) * mm});
            skLineSegment(sketch, "E10.138.1", {"start": v(1.2, -51.7) * mm, "end": v(3.6, -51.53) * mm});
            skLineSegment(sketch, "E10.138.2", {"start": v(3.43, -49.12) * mm, "end": v(1.2, -51.7) * mm});
            skLineSegment(sketch, "E10.139.0", {"start": v(4.8, -51.43) * mm, "end": v(4.58, -49.03) * mm});
            skLineSegment(sketch, "E10.139.1", {"start": v(2.4, -51.65) * mm, "end": v(4.8, -51.43) * mm});
            skLineSegment(sketch, "E10.139.2", {"start": v(4.58, -49.03) * mm, "end": v(2.4, -51.65) * mm});
            skLineSegment(sketch, "E10.140.0", {"start": v(6, -51.3) * mm, "end": v(5.72, -48.9) * mm});
            skLineSegment(sketch, "E10.140.1", {"start": v(3.6, -51.58) * mm, "end": v(6, -51.3) * mm});
            skLineSegment(sketch, "E10.140.2", {"start": v(5.72, -48.9) * mm, "end": v(3.6, -51.58) * mm});
            skLineSegment(sketch, "E10.141.0", {"start": v(7.19, -51.15) * mm, "end": v(6.85, -48.76) * mm});
            skLineSegment(sketch, "E10.141.1", {"start": v(4.8, -51.49) * mm, "end": v(7.19, -51.15) * mm});
            skLineSegment(sketch, "E10.141.2", {"start": v(6.85, -48.76) * mm, "end": v(4.8, -51.49) * mm});
            skLineSegment(sketch, "E10.142.0", {"start": v(8.38, -50.97) * mm, "end": v(7.99, -48.59) * mm});
            skLineSegment(sketch, "E10.142.1", {"start": v(6, -51.36) * mm, "end": v(8.38, -50.97) * mm});
            skLineSegment(sketch, "E10.142.2", {"start": v(7.99, -48.59) * mm, "end": v(6, -51.36) * mm});
            skLineSegment(sketch, "E10.143.0", {"start": v(9.56, -50.76) * mm, "end": v(9.11, -48.39) * mm});
            skLineSegment(sketch, "E10.143.1", {"start": v(7.19, -51.2) * mm, "end": v(9.56, -50.76) * mm});
            skLineSegment(sketch, "E10.143.2", {"start": v(9.11, -48.39) * mm, "end": v(7.19, -51.2) * mm});
            skLineSegment(sketch, "E10.144.0", {"start": v(10.74, -50.52) * mm, "end": v(10.24, -48.16) * mm});
            skLineSegment(sketch, "E10.144.1", {"start": v(8.38, -51.03) * mm, "end": v(10.74, -50.52) * mm});
            skLineSegment(sketch, "E10.144.2", {"start": v(10.24, -48.16) * mm, "end": v(8.38, -51.03) * mm});
            skLineSegment(sketch, "E10.145.0", {"start": v(11.91, -50.26) * mm, "end": v(11.36, -47.91) * mm});
            skLineSegment(sketch, "E10.145.1", {"start": v(9.56, -50.82) * mm, "end": v(11.91, -50.26) * mm});
            skLineSegment(sketch, "E10.145.2", {"start": v(11.36, -47.91) * mm, "end": v(9.56, -50.82) * mm});
            skLineSegment(sketch, "E10.146.0", {"start": v(13.08, -49.97) * mm, "end": v(12.47, -47.64) * mm});
            skLineSegment(sketch, "E10.146.1", {"start": v(10.74, -50.58) * mm, "end": v(13.08, -49.97) * mm});
            skLineSegment(sketch, "E10.146.2", {"start": v(12.47, -47.64) * mm, "end": v(10.74, -50.58) * mm});
            skLineSegment(sketch, "E10.147.0", {"start": v(14.24, -49.65) * mm, "end": v(13.57, -47.33) * mm});
            skLineSegment(sketch, "E10.147.1", {"start": v(11.92, -50.32) * mm, "end": v(14.24, -49.65) * mm});
            skLineSegment(sketch, "E10.147.2", {"start": v(13.57, -47.33) * mm, "end": v(11.92, -50.32) * mm});
            skLineSegment(sketch, "E10.148.0", {"start": v(15.39, -49.3) * mm, "end": v(14.67, -47) * mm});
            skLineSegment(sketch, "E10.148.1", {"start": v(13.09, -50.03) * mm, "end": v(15.39, -49.3) * mm});
            skLineSegment(sketch, "E10.148.2", {"start": v(14.67, -47) * mm, "end": v(13.09, -50.03) * mm});
            skLineSegment(sketch, "E10.149.0", {"start": v(16.53, -48.94) * mm, "end": v(15.76, -46.65) * mm});
            skLineSegment(sketch, "E10.149.1", {"start": v(14.25, -49.7) * mm, "end": v(16.53, -48.94) * mm});
            skLineSegment(sketch, "E10.149.2", {"start": v(15.76, -46.65) * mm, "end": v(14.25, -49.7) * mm});
            skLineSegment(sketch, "E10.150.0", {"start": v(17.67, -48.54) * mm, "end": v(16.84, -46.27) * mm});
            skLineSegment(sketch, "E10.150.1", {"start": v(15.4, -49.36) * mm, "end": v(17.67, -48.54) * mm});
            skLineSegment(sketch, "E10.150.2", {"start": v(16.84, -46.27) * mm, "end": v(15.4, -49.36) * mm});
            skLineSegment(sketch, "E10.151.0", {"start": v(18.8, -48.11) * mm, "end": v(17.91, -45.87) * mm});
            skLineSegment(sketch, "E10.151.1", {"start": v(16.54, -49) * mm, "end": v(18.8, -48.11) * mm});
            skLineSegment(sketch, "E10.151.2", {"start": v(17.91, -45.87) * mm, "end": v(16.54, -49) * mm});
            skLineSegment(sketch, "E10.152.0", {"start": v(19.9, -47.66) * mm, "end": v(18.98, -45.44) * mm});
            skLineSegment(sketch, "E10.152.1", {"start": v(17.68, -48.6) * mm, "end": v(19.9, -47.66) * mm});
            skLineSegment(sketch, "E10.152.2", {"start": v(18.98, -45.44) * mm, "end": v(17.68, -48.6) * mm});
            skLineSegment(sketch, "E10.153.0", {"start": v(21, -47.19) * mm, "end": v(20.03, -44.98) * mm});
            skLineSegment(sketch, "E10.153.1", {"start": v(18.8, -48.17) * mm, "end": v(21, -47.19) * mm});
            skLineSegment(sketch, "E10.153.2", {"start": v(20.03, -44.98) * mm, "end": v(18.8, -48.17) * mm});
            skLineSegment(sketch, "E10.154.0", {"start": v(22.1, -46.69) * mm, "end": v(21.07, -44.5) * mm});
            skLineSegment(sketch, "E10.154.1", {"start": v(19.92, -47.72) * mm, "end": v(22.1, -46.69) * mm});
            skLineSegment(sketch, "E10.154.2", {"start": v(21.07, -44.5) * mm, "end": v(19.92, -47.72) * mm});
            skLineSegment(sketch, "E10.155.0", {"start": v(23.18, -46.16) * mm, "end": v(22.1, -44) * mm});
            skLineSegment(sketch, "E10.155.1", {"start": v(21.03, -47.24) * mm, "end": v(23.18, -46.16) * mm});
            skLineSegment(sketch, "E10.155.2", {"start": v(22.1, -44) * mm, "end": v(21.03, -47.24) * mm});
            skLineSegment(sketch, "E10.156.0", {"start": v(24.25, -45.6) * mm, "end": v(23.12, -43.48) * mm});
            skLineSegment(sketch, "E10.156.1", {"start": v(22.12, -46.74) * mm, "end": v(24.25, -45.6) * mm});
            skLineSegment(sketch, "E10.156.2", {"start": v(23.12, -43.48) * mm, "end": v(22.12, -46.74) * mm});
            skLineSegment(sketch, "E10.157.0", {"start": v(25.3, -45.03) * mm, "end": v(24.12, -42.93) * mm});
            skLineSegment(sketch, "E10.157.1", {"start": v(23.2, -46.21) * mm, "end": v(25.3, -45.03) * mm});
            skLineSegment(sketch, "E10.157.2", {"start": v(24.12, -42.93) * mm, "end": v(23.2, -46.21) * mm});
            skLineSegment(sketch, "E10.158.0", {"start": v(26.35, -44.43) * mm, "end": v(25.11, -42.35) * mm});
            skLineSegment(sketch, "E10.158.1", {"start": v(24.27, -45.66) * mm, "end": v(26.35, -44.43) * mm});
            skLineSegment(sketch, "E10.158.2", {"start": v(25.11, -42.35) * mm, "end": v(24.27, -45.66) * mm});
            skLineSegment(sketch, "E10.159.0", {"start": v(27.37, -43.8) * mm, "end": v(26.1, -41.76) * mm});
            skLineSegment(sketch, "E10.159.1", {"start": v(25.33, -45.08) * mm, "end": v(27.37, -43.8) * mm});
            skLineSegment(sketch, "E10.159.2", {"start": v(26.1, -41.76) * mm, "end": v(25.33, -45.08) * mm});
            skLineSegment(sketch, "E10.160.0", {"start": v(28.38, -43.16) * mm, "end": v(27.06, -41.14) * mm});
            skLineSegment(sketch, "E10.160.1", {"start": v(26.37, -44.48) * mm, "end": v(28.38, -43.16) * mm});
            skLineSegment(sketch, "E10.160.2", {"start": v(27.06, -41.14) * mm, "end": v(26.37, -44.48) * mm});
            skLineSegment(sketch, "E10.161.0", {"start": v(29.38, -42.48) * mm, "end": v(28, -40.5) * mm});
            skLineSegment(sketch, "E10.161.1", {"start": v(27.4, -43.86) * mm, "end": v(29.38, -42.48) * mm});
            skLineSegment(sketch, "E10.161.2", {"start": v(28, -40.5) * mm, "end": v(27.4, -43.86) * mm});
            skLineSegment(sketch, "E10.162.0", {"start": v(30.36, -41.79) * mm, "end": v(28.94, -39.84) * mm});
            skLineSegment(sketch, "E10.162.1", {"start": v(28.4, -43.2) * mm, "end": v(30.36, -41.79) * mm});
            skLineSegment(sketch, "E10.162.2", {"start": v(28.94, -39.84) * mm, "end": v(28.4, -43.2) * mm});
            skLineSegment(sketch, "E10.163.0", {"start": v(31.33, -41.07) * mm, "end": v(29.86, -39.15) * mm});
            skLineSegment(sketch, "E10.163.1", {"start": v(29.4, -42.53) * mm, "end": v(31.33, -41.07) * mm});
            skLineSegment(sketch, "E10.163.2", {"start": v(29.86, -39.15) * mm, "end": v(29.4, -42.53) * mm});
            skLineSegment(sketch, "E10.164.0", {"start": v(32.27, -40.33) * mm, "end": v(30.77, -38.45) * mm});
            skLineSegment(sketch, "E10.164.1", {"start": v(30.39, -41.84) * mm, "end": v(32.27, -40.33) * mm});
            skLineSegment(sketch, "E10.164.2", {"start": v(30.77, -38.45) * mm, "end": v(30.39, -41.84) * mm});
            skLineSegment(sketch, "E10.165.0", {"start": v(33.2, -39.57) * mm, "end": v(31.65, -37.72) * mm});
            skLineSegment(sketch, "E10.165.1", {"start": v(31.35, -41.12) * mm, "end": v(33.2, -39.57) * mm});
            skLineSegment(sketch, "E10.165.2", {"start": v(31.65, -37.72) * mm, "end": v(31.35, -41.12) * mm});
            skLineSegment(sketch, "E10.166.0", {"start": v(34.11, -38.79) * mm, "end": v(32.52, -36.97) * mm});
            skLineSegment(sketch, "E10.166.1", {"start": v(32.3, -40.38) * mm, "end": v(34.11, -38.79) * mm});
            skLineSegment(sketch, "E10.166.2", {"start": v(32.52, -36.97) * mm, "end": v(32.3, -40.38) * mm});
            skLineSegment(sketch, "E10.167.0", {"start": v(35, -37.98) * mm, "end": v(33.37, -36.2) * mm});
            skLineSegment(sketch, "E10.167.1", {"start": v(33.23, -39.62) * mm, "end": v(35, -37.98) * mm});
            skLineSegment(sketch, "E10.167.2", {"start": v(33.37, -36.2) * mm, "end": v(33.23, -39.62) * mm});
            skLineSegment(sketch, "E10.168.0", {"start": v(35.88, -37.16) * mm, "end": v(34.2, -35.42) * mm});
            skLineSegment(sketch, "E10.168.1", {"start": v(34.15, -38.83) * mm, "end": v(35.88, -37.16) * mm});
            skLineSegment(sketch, "E10.168.2", {"start": v(34.2, -35.42) * mm, "end": v(34.15, -38.83) * mm});
            skLineSegment(sketch, "E10.169.0", {"start": v(36.74, -36.31) * mm, "end": v(35.02, -34.62) * mm});
            skLineSegment(sketch, "E10.169.1", {"start": v(35.04, -38.03) * mm, "end": v(36.74, -36.31) * mm});
            skLineSegment(sketch, "E10.169.2", {"start": v(35.02, -34.62) * mm, "end": v(35.04, -38.03) * mm});
            skLineSegment(sketch, "E10.170.0", {"start": v(37.57, -35.45) * mm, "end": v(35.82, -33.8) * mm});
            skLineSegment(sketch, "E10.170.1", {"start": v(35.92, -37.2) * mm, "end": v(37.57, -35.45) * mm});
            skLineSegment(sketch, "E10.170.2", {"start": v(35.82, -33.8) * mm, "end": v(35.92, -37.2) * mm});
            skLineSegment(sketch, "E10.171.0", {"start": v(38.39, -34.56) * mm, "end": v(36.6, -32.95) * mm});
            skLineSegment(sketch, "E10.171.1", {"start": v(36.77, -36.36) * mm, "end": v(38.39, -34.56) * mm});
            skLineSegment(sketch, "E10.171.2", {"start": v(36.6, -32.95) * mm, "end": v(36.77, -36.36) * mm});
            skLineSegment(sketch, "E10.172.0", {"start": v(39.18, -33.66) * mm, "end": v(37.35, -32.09) * mm});
            skLineSegment(sketch, "E10.172.1", {"start": v(37.6, -35.5) * mm, "end": v(39.18, -33.66) * mm});
            skLineSegment(sketch, "E10.172.2", {"start": v(37.35, -32.09) * mm, "end": v(37.6, -35.5) * mm});
            skLineSegment(sketch, "E10.173.0", {"start": v(39.95, -32.74) * mm, "end": v(38.09, -31.21) * mm});
            skLineSegment(sketch, "E10.173.1", {"start": v(38.42, -34.6) * mm, "end": v(39.95, -32.74) * mm});
            skLineSegment(sketch, "E10.173.2", {"start": v(38.09, -31.21) * mm, "end": v(38.42, -34.6) * mm});
            skLineSegment(sketch, "E10.174.0", {"start": v(40.7, -31.8) * mm, "end": v(38.8, -30.32) * mm});
            skLineSegment(sketch, "E10.174.1", {"start": v(39.22, -33.7) * mm, "end": v(40.7, -31.8) * mm});
            skLineSegment(sketch, "E10.174.2", {"start": v(38.8, -30.32) * mm, "end": v(39.22, -33.7) * mm});
            skLineSegment(sketch, "E10.175.0", {"start": v(41.43, -30.85) * mm, "end": v(39.5, -29.4) * mm});
            skLineSegment(sketch, "E10.175.1", {"start": v(40, -32.78) * mm, "end": v(41.43, -30.85) * mm});
            skLineSegment(sketch, "E10.175.2", {"start": v(39.5, -29.4) * mm, "end": v(40, -32.78) * mm});
            skLineSegment(sketch, "E10.176.0", {"start": v(42.14, -29.87) * mm, "end": v(40.17, -28.48) * mm});
            skLineSegment(sketch, "E10.176.1", {"start": v(40.74, -31.84) * mm, "end": v(42.14, -29.87) * mm});
            skLineSegment(sketch, "E10.176.2", {"start": v(40.17, -28.48) * mm, "end": v(40.74, -31.84) * mm});
            skLineSegment(sketch, "E10.177.0", {"start": v(42.82, -28.88) * mm, "end": v(40.82, -27.54) * mm});
            skLineSegment(sketch, "E10.177.1", {"start": v(41.47, -30.88) * mm, "end": v(42.82, -28.88) * mm});
            skLineSegment(sketch, "E10.177.2", {"start": v(40.82, -27.54) * mm, "end": v(41.47, -30.88) * mm});
            skLineSegment(sketch, "E10.178.0", {"start": v(43.48, -27.88) * mm, "end": v(41.45, -26.58) * mm});
            skLineSegment(sketch, "E10.178.1", {"start": v(42.18, -29.91) * mm, "end": v(43.48, -27.88) * mm});
            skLineSegment(sketch, "E10.178.2", {"start": v(41.45, -26.58) * mm, "end": v(42.18, -29.91) * mm});
            skLineSegment(sketch, "E10.179.0", {"start": v(44.12, -26.86) * mm, "end": v(42.06, -25.6) * mm});
            skLineSegment(sketch, "E10.179.1", {"start": v(42.87, -28.92) * mm, "end": v(44.12, -26.86) * mm});
            skLineSegment(sketch, "E10.179.2", {"start": v(42.06, -25.6) * mm, "end": v(42.87, -28.92) * mm});
            skLineSegment(sketch, "E10.180.0", {"start": v(44.73, -25.83) * mm, "end": v(42.64, -24.62) * mm});
            skLineSegment(sketch, "E10.180.1", {"start": v(43.53, -27.92) * mm, "end": v(44.73, -25.83) * mm});
            skLineSegment(sketch, "E10.180.2", {"start": v(42.64, -24.62) * mm, "end": v(43.53, -27.92) * mm});
            skLineSegment(sketch, "E10.181.0", {"start": v(45.32, -24.78) * mm, "end": v(43.2, -23.62) * mm});
            skLineSegment(sketch, "E10.181.1", {"start": v(44.16, -26.9) * mm, "end": v(45.32, -24.78) * mm});
            skLineSegment(sketch, "E10.181.2", {"start": v(43.2, -23.62) * mm, "end": v(44.16, -26.9) * mm});
            skLineSegment(sketch, "E10.182.0", {"start": v(45.89, -23.72) * mm, "end": v(43.74, -22.6) * mm});
            skLineSegment(sketch, "E10.182.1", {"start": v(44.78, -25.86) * mm, "end": v(45.89, -23.72) * mm});
            skLineSegment(sketch, "E10.182.2", {"start": v(43.74, -22.6) * mm, "end": v(44.78, -25.86) * mm});
            skLineSegment(sketch, "E10.183.0", {"start": v(46.43, -22.64) * mm, "end": v(44.26, -21.59) * mm});
            skLineSegment(sketch, "E10.183.1", {"start": v(45.37, -24.81) * mm, "end": v(46.43, -22.64) * mm});
            skLineSegment(sketch, "E10.183.2", {"start": v(44.26, -21.59) * mm, "end": v(45.37, -24.81) * mm});
            skLineSegment(sketch, "E10.184.0", {"start": v(46.94, -21.56) * mm, "end": v(44.75, -20.55) * mm});
            skLineSegment(sketch, "E10.184.1", {"start": v(45.93, -23.75) * mm, "end": v(46.94, -21.56) * mm});
            skLineSegment(sketch, "E10.184.2", {"start": v(44.75, -20.55) * mm, "end": v(45.93, -23.75) * mm});
            skLineSegment(sketch, "E10.185.0", {"start": v(47.43, -20.46) * mm, "end": v(45.21, -19.5) * mm});
            skLineSegment(sketch, "E10.185.1", {"start": v(46.47, -22.67) * mm, "end": v(47.43, -20.46) * mm});
            skLineSegment(sketch, "E10.185.2", {"start": v(45.21, -19.5) * mm, "end": v(46.47, -22.67) * mm});
            skLineSegment(sketch, "E10.186.0", {"start": v(47.9, -19.35) * mm, "end": v(45.66, -18.45) * mm});
            skLineSegment(sketch, "E10.186.1", {"start": v(46.99, -21.59) * mm, "end": v(47.9, -19.35) * mm});
            skLineSegment(sketch, "E10.186.2", {"start": v(45.66, -18.45) * mm, "end": v(46.99, -21.59) * mm});
            skLineSegment(sketch, "E10.187.0", {"start": v(48.33, -18.23) * mm, "end": v(46.07, -17.38) * mm});
            skLineSegment(sketch, "E10.187.1", {"start": v(47.48, -20.49) * mm, "end": v(48.33, -18.23) * mm});
            skLineSegment(sketch, "E10.187.2", {"start": v(46.07, -17.38) * mm, "end": v(47.48, -20.49) * mm});
            skLineSegment(sketch, "E10.188.0", {"start": v(48.74, -17.1) * mm, "end": v(46.46, -16.3) * mm});
            skLineSegment(sketch, "E10.188.1", {"start": v(47.94, -19.38) * mm, "end": v(48.74, -17.1) * mm});
            skLineSegment(sketch, "E10.188.2", {"start": v(46.46, -16.3) * mm, "end": v(47.94, -19.38) * mm});
            skLineSegment(sketch, "E10.189.0", {"start": v(49.13, -15.96) * mm, "end": v(46.83, -15.22) * mm});
            skLineSegment(sketch, "E10.189.1", {"start": v(48.38, -18.26) * mm, "end": v(49.13, -15.96) * mm});
            skLineSegment(sketch, "E10.189.2", {"start": v(46.83, -15.22) * mm, "end": v(48.38, -18.26) * mm});
            skLineSegment(sketch, "E10.190.0", {"start": v(49.48, -14.81) * mm, "end": v(47.17, -14.12) * mm});
            skLineSegment(sketch, "E10.190.1", {"start": v(48.8, -17.13) * mm, "end": v(49.48, -14.81) * mm});
            skLineSegment(sketch, "E10.190.2", {"start": v(47.17, -14.12) * mm, "end": v(48.8, -17.13) * mm});
            skLineSegment(sketch, "E10.191.0", {"start": v(49.81, -13.66) * mm, "end": v(47.49, -13.02) * mm});
            skLineSegment(sketch, "E10.191.1", {"start": v(49.18, -15.99) * mm, "end": v(49.81, -13.66) * mm});
            skLineSegment(sketch, "E10.191.2", {"start": v(47.49, -13.02) * mm, "end": v(49.18, -15.99) * mm});
            skLineSegment(sketch, "E10.192.0", {"start": v(50.12, -12.5) * mm, "end": v(47.78, -11.91) * mm});
            skLineSegment(sketch, "E10.192.1", {"start": v(49.54, -14.84) * mm, "end": v(50.12, -12.5) * mm});
            skLineSegment(sketch, "E10.192.2", {"start": v(47.78, -11.91) * mm, "end": v(49.54, -14.84) * mm});
            skLineSegment(sketch, "E10.193.0", {"start": v(50.4, -11.33) * mm, "end": v(48.04, -10.8) * mm});
            skLineSegment(sketch, "E10.193.1", {"start": v(49.87, -13.68) * mm, "end": v(50.4, -11.33) * mm});
            skLineSegment(sketch, "E10.193.2", {"start": v(48.04, -10.8) * mm, "end": v(49.87, -13.68) * mm});
            skLineSegment(sketch, "E10.194.0", {"start": v(50.65, -10.15) * mm, "end": v(48.28, -9.68) * mm});
            skLineSegment(sketch, "E10.194.1", {"start": v(50.17, -12.52) * mm, "end": v(50.65, -10.15) * mm});
            skLineSegment(sketch, "E10.194.2", {"start": v(48.28, -9.68) * mm, "end": v(50.17, -12.52) * mm});
            skLineSegment(sketch, "E10.195.0", {"start": v(50.87, -8.97) * mm, "end": v(48.5, -8.55) * mm});
            skLineSegment(sketch, "E10.195.1", {"start": v(50.45, -11.35) * mm, "end": v(50.87, -8.97) * mm});
            skLineSegment(sketch, "E10.195.2", {"start": v(48.5, -8.55) * mm, "end": v(50.45, -11.35) * mm});
            skLineSegment(sketch, "E10.196.0", {"start": v(51.06, -7.78) * mm, "end": v(48.68, -7.42) * mm});
            skLineSegment(sketch, "E10.196.1", {"start": v(50.7, -10.17) * mm, "end": v(51.06, -7.78) * mm});
            skLineSegment(sketch, "E10.196.2", {"start": v(48.68, -7.42) * mm, "end": v(50.7, -10.17) * mm});
            skLineSegment(sketch, "E10.197.0", {"start": v(51.23, -6.6) * mm, "end": v(48.84, -6.29) * mm});
            skLineSegment(sketch, "E10.197.1", {"start": v(50.92, -8.99) * mm, "end": v(51.23, -6.6) * mm});
            skLineSegment(sketch, "E10.197.2", {"start": v(48.84, -6.29) * mm, "end": v(50.92, -8.99) * mm});
            skLineSegment(sketch, "E10.198.0", {"start": v(51.37, -5.4) * mm, "end": v(48.97, -5.15) * mm});
            skLineSegment(sketch, "E10.198.1", {"start": v(51.12, -7.8) * mm, "end": v(51.37, -5.4) * mm});
            skLineSegment(sketch, "E10.198.2", {"start": v(48.97, -5.15) * mm, "end": v(51.12, -7.8) * mm});
            skLineSegment(sketch, "E10.199.0", {"start": v(51.48, -4.2) * mm, "end": v(49.08, -4) * mm});
            skLineSegment(sketch, "E10.199.1", {"start": v(51.29, -6.6) * mm, "end": v(51.48, -4.2) * mm});
            skLineSegment(sketch, "E10.199.2", {"start": v(49.08, -4) * mm, "end": v(51.29, -6.6) * mm});
            skLineSegment(sketch, "E10.200.0", {"start": v(51.57, -3) * mm, "end": v(49.16, -2.86) * mm});
            skLineSegment(sketch, "E10.200.1", {"start": v(51.43, -5.41) * mm, "end": v(51.57, -3) * mm});
            skLineSegment(sketch, "E10.200.2", {"start": v(49.16, -2.86) * mm, "end": v(51.43, -5.41) * mm});
            skLineSegment(sketch, "E10.201.0", {"start": v(51.62, -1.8) * mm, "end": v(49.21, -1.72) * mm});
            skLineSegment(sketch, "E10.201.1", {"start": v(51.54, -4.21) * mm, "end": v(51.62, -1.8) * mm});
            skLineSegment(sketch, "E10.201.2", {"start": v(49.21, -1.72) * mm, "end": v(51.54, -4.21) * mm});
            skLineSegment(sketch, "E10.202.0", {"start": v(51.65, -0.6) * mm, "end": v(49.24, -0.57) * mm});
            skLineSegment(sketch, "E10.202.1", {"start": v(51.62, -3.01) * mm, "end": v(51.65, -0.6) * mm});
            skLineSegment(sketch, "E10.202.2", {"start": v(49.24, -0.57) * mm, "end": v(51.62, -3.01) * mm});
            skLineSegment(sketch, "E10.203.0", {"start": v(51.65, 0.6) * mm, "end": v(49.24, 0.57) * mm});
            skLineSegment(sketch, "E10.203.1", {"start": v(51.68, -1.81) * mm, "end": v(51.65, 0.6) * mm});
            skLineSegment(sketch, "E10.203.2", {"start": v(49.24, 0.57) * mm, "end": v(51.68, -1.81) * mm});
            skLineSegment(sketch, "E10.204.0", {"start": v(51.62, 1.8) * mm, "end": v(49.21, 1.72) * mm});
            skLineSegment(sketch, "E10.204.1", {"start": v(51.7, -0.6) * mm, "end": v(51.62, 1.8) * mm});
            skLineSegment(sketch, "E10.204.2", {"start": v(49.21, 1.72) * mm, "end": v(51.7, -0.6) * mm});
            skLineSegment(sketch, "E10.205.0", {"start": v(51.57, 3) * mm, "end": v(49.16, 2.86) * mm});
            skLineSegment(sketch, "E10.205.1", {"start": v(51.7, 0.6) * mm, "end": v(51.57, 3) * mm});
            skLineSegment(sketch, "E10.205.2", {"start": v(49.16, 2.86) * mm, "end": v(51.7, 0.6) * mm});
            skLineSegment(sketch, "E10.206.0", {"start": v(51.48, 4.2) * mm, "end": v(49.08, 4) * mm});
            skLineSegment(sketch, "E10.206.1", {"start": v(51.68, 1.8) * mm, "end": v(51.48, 4.2) * mm});
            skLineSegment(sketch, "E10.206.2", {"start": v(49.08, 4) * mm, "end": v(51.68, 1.8) * mm});
            skLineSegment(sketch, "E10.207.0", {"start": v(51.37, 5.4) * mm, "end": v(48.97, 5.15) * mm});
            skLineSegment(sketch, "E10.207.1", {"start": v(51.62, 3) * mm, "end": v(51.37, 5.4) * mm});
            skLineSegment(sketch, "E10.207.2", {"start": v(48.97, 5.15) * mm, "end": v(51.62, 3) * mm});
            skLineSegment(sketch, "E10.208.0", {"start": v(51.23, 6.6) * mm, "end": v(48.84, 6.29) * mm});
            skLineSegment(sketch, "E10.208.1", {"start": v(51.54, 4.2) * mm, "end": v(51.23, 6.6) * mm});
            skLineSegment(sketch, "E10.208.2", {"start": v(48.84, 6.29) * mm, "end": v(51.54, 4.2) * mm});
            skLineSegment(sketch, "E10.209.0", {"start": v(51.06, 7.78) * mm, "end": v(48.68, 7.42) * mm});
            skLineSegment(sketch, "E10.209.1", {"start": v(51.43, 5.4) * mm, "end": v(51.06, 7.78) * mm});
            skLineSegment(sketch, "E10.209.2", {"start": v(48.68, 7.42) * mm, "end": v(51.43, 5.4) * mm});
            skLineSegment(sketch, "E10.210.0", {"start": v(50.87, 8.97) * mm, "end": v(48.5, 8.55) * mm});
            skLineSegment(sketch, "E10.210.1", {"start": v(51.29, 6.6) * mm, "end": v(50.87, 8.97) * mm});
            skLineSegment(sketch, "E10.210.2", {"start": v(48.5, 8.55) * mm, "end": v(51.29, 6.6) * mm});
            skLineSegment(sketch, "E10.211.0", {"start": v(50.65, 10.15) * mm, "end": v(48.28, 9.68) * mm});
            skLineSegment(sketch, "E10.211.1", {"start": v(51.12, 7.79) * mm, "end": v(50.65, 10.15) * mm});
            skLineSegment(sketch, "E10.211.2", {"start": v(48.28, 9.68) * mm, "end": v(51.12, 7.79) * mm});
            skLineSegment(sketch, "E10.212.0", {"start": v(50.4, 11.33) * mm, "end": v(48.04, 10.8) * mm});
            skLineSegment(sketch, "E10.212.1", {"start": v(50.93, 8.97) * mm, "end": v(50.4, 11.33) * mm});
            skLineSegment(sketch, "E10.212.2", {"start": v(48.04, 10.8) * mm, "end": v(50.93, 8.97) * mm});
            skLineSegment(sketch, "E10.213.0", {"start": v(50.12, 12.5) * mm, "end": v(47.78, 11.91) * mm});
            skLineSegment(sketch, "E10.213.1", {"start": v(50.7, 10.16) * mm, "end": v(50.12, 12.5) * mm});
            skLineSegment(sketch, "E10.213.2", {"start": v(47.78, 11.91) * mm, "end": v(50.7, 10.16) * mm});
            skLineSegment(sketch, "E10.214.0", {"start": v(49.81, 13.66) * mm, "end": v(47.49, 13.02) * mm});
            skLineSegment(sketch, "E10.214.1", {"start": v(50.45, 11.33) * mm, "end": v(49.81, 13.66) * mm});
            skLineSegment(sketch, "E10.214.2", {"start": v(47.49, 13.02) * mm, "end": v(50.45, 11.33) * mm});
            skLineSegment(sketch, "E10.215.0", {"start": v(49.48, 14.81) * mm, "end": v(47.17, 14.12) * mm});
            skLineSegment(sketch, "E10.215.1", {"start": v(50.18, 12.5) * mm, "end": v(49.48, 14.81) * mm});
            skLineSegment(sketch, "E10.215.2", {"start": v(47.17, 14.12) * mm, "end": v(50.18, 12.5) * mm});
            skLineSegment(sketch, "E10.216.0", {"start": v(49.13, 15.96) * mm, "end": v(46.83, 15.22) * mm});
            skLineSegment(sketch, "E10.216.1", {"start": v(49.87, 13.67) * mm, "end": v(49.13, 15.96) * mm});
            skLineSegment(sketch, "E10.216.2", {"start": v(46.83, 15.22) * mm, "end": v(49.87, 13.67) * mm});
            skLineSegment(sketch, "E10.217.0", {"start": v(48.74, 17.1) * mm, "end": v(46.46, 16.3) * mm});
            skLineSegment(sketch, "E10.217.1", {"start": v(49.54, 14.82) * mm, "end": v(48.74, 17.1) * mm});
            skLineSegment(sketch, "E10.217.2", {"start": v(46.46, 16.3) * mm, "end": v(49.54, 14.82) * mm});
            skLineSegment(sketch, "E10.218.0", {"start": v(48.33, 18.23) * mm, "end": v(46.07, 17.38) * mm});
            skLineSegment(sketch, "E10.218.1", {"start": v(49.18, 15.97) * mm, "end": v(48.33, 18.23) * mm});
            skLineSegment(sketch, "E10.218.2", {"start": v(46.07, 17.38) * mm, "end": v(49.18, 15.97) * mm});
            skLineSegment(sketch, "E10.219.0", {"start": v(47.9, 19.35) * mm, "end": v(45.66, 18.45) * mm});
            skLineSegment(sketch, "E10.219.1", {"start": v(48.8, 17.11) * mm, "end": v(47.9, 19.35) * mm});
            skLineSegment(sketch, "E10.219.2", {"start": v(45.66, 18.45) * mm, "end": v(48.8, 17.11) * mm});
            skLineSegment(sketch, "E10.220.0", {"start": v(47.43, 20.46) * mm, "end": v(45.21, 19.5) * mm});
            skLineSegment(sketch, "E10.220.1", {"start": v(48.38, 18.24) * mm, "end": v(47.43, 20.46) * mm});
            skLineSegment(sketch, "E10.220.2", {"start": v(45.21, 19.5) * mm, "end": v(48.38, 18.24) * mm});
            skLineSegment(sketch, "E10.221.0", {"start": v(46.94, 21.56) * mm, "end": v(44.75, 20.55) * mm});
            skLineSegment(sketch, "E10.221.1", {"start": v(47.95, 19.36) * mm, "end": v(46.94, 21.56) * mm});
            skLineSegment(sketch, "E10.221.2", {"start": v(44.75, 20.55) * mm, "end": v(47.95, 19.36) * mm});
            skLineSegment(sketch, "E10.222.0", {"start": v(46.43, 22.64) * mm, "end": v(44.26, 21.59) * mm});
            skLineSegment(sketch, "E10.222.1", {"start": v(47.48, 20.48) * mm, "end": v(46.43, 22.64) * mm});
            skLineSegment(sketch, "E10.222.2", {"start": v(44.26, 21.59) * mm, "end": v(47.48, 20.48) * mm});
            skLineSegment(sketch, "E10.223.0", {"start": v(45.89, 23.72) * mm, "end": v(43.74, 22.6) * mm});
            skLineSegment(sketch, "E10.223.1", {"start": v(47, 21.57) * mm, "end": v(45.89, 23.72) * mm});
            skLineSegment(sketch, "E10.223.2", {"start": v(43.74, 22.6) * mm, "end": v(47, 21.57) * mm});
            skLineSegment(sketch, "E10.224.0", {"start": v(45.32, 24.78) * mm, "end": v(43.2, 23.62) * mm});
            skLineSegment(sketch, "E10.224.1", {"start": v(46.48, 22.66) * mm, "end": v(45.32, 24.78) * mm});
            skLineSegment(sketch, "E10.224.2", {"start": v(43.2, 23.62) * mm, "end": v(46.48, 22.66) * mm});
            skLineSegment(sketch, "E10.225.0", {"start": v(44.73, 25.83) * mm, "end": v(42.64, 24.62) * mm});
            skLineSegment(sketch, "E10.225.1", {"start": v(45.94, 23.74) * mm, "end": v(44.73, 25.83) * mm});
            skLineSegment(sketch, "E10.225.2", {"start": v(42.64, 24.62) * mm, "end": v(45.94, 23.74) * mm});
            skLineSegment(sketch, "E10.226.0", {"start": v(44.12, 26.86) * mm, "end": v(42.06, 25.6) * mm});
            skLineSegment(sketch, "E10.226.1", {"start": v(45.37, 24.8) * mm, "end": v(44.12, 26.86) * mm});
            skLineSegment(sketch, "E10.226.2", {"start": v(42.06, 25.6) * mm, "end": v(45.37, 24.8) * mm});
            skLineSegment(sketch, "E10.227.0", {"start": v(43.48, 27.88) * mm, "end": v(41.45, 26.58) * mm});
            skLineSegment(sketch, "E10.227.1", {"start": v(44.79, 25.85) * mm, "end": v(43.48, 27.88) * mm});
            skLineSegment(sketch, "E10.227.2", {"start": v(41.45, 26.58) * mm, "end": v(44.79, 25.85) * mm});
            skLineSegment(sketch, "E10.228.0", {"start": v(42.82, 28.88) * mm, "end": v(40.82, 27.54) * mm});
            skLineSegment(sketch, "E10.228.1", {"start": v(44.17, 26.88) * mm, "end": v(42.82, 28.88) * mm});
            skLineSegment(sketch, "E10.228.2", {"start": v(40.82, 27.54) * mm, "end": v(44.17, 26.88) * mm});
            skLineSegment(sketch, "E10.229.0", {"start": v(42.14, 29.87) * mm, "end": v(40.17, 28.48) * mm});
            skLineSegment(sketch, "E10.229.1", {"start": v(43.53, 27.9) * mm, "end": v(42.14, 29.87) * mm});
            skLineSegment(sketch, "E10.229.2", {"start": v(40.17, 28.48) * mm, "end": v(43.53, 27.9) * mm});
            skLineSegment(sketch, "E10.230.0", {"start": v(41.43, 30.85) * mm, "end": v(39.5, 29.4) * mm});
            skLineSegment(sketch, "E10.230.1", {"start": v(42.87, 28.91) * mm, "end": v(41.43, 30.85) * mm});
            skLineSegment(sketch, "E10.230.2", {"start": v(39.5, 29.4) * mm, "end": v(42.87, 28.91) * mm});
            skLineSegment(sketch, "E10.231.0", {"start": v(40.7, 31.8) * mm, "end": v(38.8, 30.32) * mm});
            skLineSegment(sketch, "E10.231.1", {"start": v(42.19, 29.9) * mm, "end": v(40.7, 31.8) * mm});
            skLineSegment(sketch, "E10.231.2", {"start": v(38.8, 30.32) * mm, "end": v(42.19, 29.9) * mm});
            skLineSegment(sketch, "E10.232.0", {"start": v(39.95, 32.74) * mm, "end": v(38.09, 31.21) * mm});
            skLineSegment(sketch, "E10.232.1", {"start": v(41.48, 30.87) * mm, "end": v(39.95, 32.74) * mm});
            skLineSegment(sketch, "E10.232.2", {"start": v(38.09, 31.21) * mm, "end": v(41.48, 30.87) * mm});
            skLineSegment(sketch, "E10.233.0", {"start": v(39.18, 33.66) * mm, "end": v(37.35, 32.09) * mm});
            skLineSegment(sketch, "E10.233.1", {"start": v(40.75, 31.83) * mm, "end": v(39.18, 33.66) * mm});
            skLineSegment(sketch, "E10.233.2", {"start": v(37.35, 32.09) * mm, "end": v(40.75, 31.83) * mm});
            skLineSegment(sketch, "E10.234.0", {"start": v(38.39, 34.56) * mm, "end": v(36.6, 32.95) * mm});
            skLineSegment(sketch, "E10.234.1", {"start": v(40, 32.77) * mm, "end": v(38.39, 34.56) * mm});
            skLineSegment(sketch, "E10.234.2", {"start": v(36.6, 32.95) * mm, "end": v(40, 32.77) * mm});
            skLineSegment(sketch, "E10.235.0", {"start": v(37.57, 35.45) * mm, "end": v(35.82, 33.8) * mm});
            skLineSegment(sketch, "E10.235.1", {"start": v(39.23, 33.7) * mm, "end": v(37.57, 35.45) * mm});
            skLineSegment(sketch, "E10.235.2", {"start": v(35.82, 33.8) * mm, "end": v(39.23, 33.7) * mm});
            skLineSegment(sketch, "E10.236.0", {"start": v(36.74, 36.31) * mm, "end": v(35.02, 34.62) * mm});
            skLineSegment(sketch, "E10.236.1", {"start": v(38.43, 34.6) * mm, "end": v(36.74, 36.31) * mm});
            skLineSegment(sketch, "E10.236.2", {"start": v(35.02, 34.62) * mm, "end": v(38.43, 34.6) * mm});
            skLineSegment(sketch, "E10.237.0", {"start": v(35.88, 37.16) * mm, "end": v(34.2, 35.42) * mm});
            skLineSegment(sketch, "E10.237.1", {"start": v(37.62, 35.48) * mm, "end": v(35.88, 37.16) * mm});
            skLineSegment(sketch, "E10.237.2", {"start": v(34.2, 35.42) * mm, "end": v(37.62, 35.48) * mm});
            skLineSegment(sketch, "E10.238.0", {"start": v(35, 37.98) * mm, "end": v(33.37, 36.2) * mm});
            skLineSegment(sketch, "E10.238.1", {"start": v(36.78, 36.35) * mm, "end": v(35, 37.98) * mm});
            skLineSegment(sketch, "E10.238.2", {"start": v(33.37, 36.2) * mm, "end": v(36.78, 36.35) * mm});
            skLineSegment(sketch, "E10.239.0", {"start": v(34.11, 38.79) * mm, "end": v(32.52, 36.97) * mm});
            skLineSegment(sketch, "E10.239.1", {"start": v(35.93, 37.2) * mm, "end": v(34.11, 38.79) * mm});
            skLineSegment(sketch, "E10.239.2", {"start": v(32.52, 36.97) * mm, "end": v(35.93, 37.2) * mm});
            skLineSegment(sketch, "E10.240.0", {"start": v(33.2, 39.57) * mm, "end": v(31.65, 37.72) * mm});
            skLineSegment(sketch, "E10.240.1", {"start": v(35.05, 38.02) * mm, "end": v(33.2, 39.57) * mm});
            skLineSegment(sketch, "E10.240.2", {"start": v(31.65, 37.72) * mm, "end": v(35.05, 38.02) * mm});
            skLineSegment(sketch, "E10.241.0", {"start": v(32.27, 40.33) * mm, "end": v(30.77, 38.45) * mm});
            skLineSegment(sketch, "E10.241.1", {"start": v(34.16, 38.82) * mm, "end": v(32.27, 40.33) * mm});
            skLineSegment(sketch, "E10.241.2", {"start": v(30.77, 38.45) * mm, "end": v(34.16, 38.82) * mm});
            skLineSegment(sketch, "E10.242.0", {"start": v(31.33, 41.07) * mm, "end": v(29.86, 39.15) * mm});
            skLineSegment(sketch, "E10.242.1", {"start": v(33.24, 39.6) * mm, "end": v(31.33, 41.07) * mm});
            skLineSegment(sketch, "E10.242.2", {"start": v(29.86, 39.15) * mm, "end": v(33.24, 39.6) * mm});
            skLineSegment(sketch, "E10.243.0", {"start": v(30.36, 41.79) * mm, "end": v(28.94, 39.84) * mm});
            skLineSegment(sketch, "E10.243.1", {"start": v(32.31, 40.37) * mm, "end": v(30.36, 41.79) * mm});
            skLineSegment(sketch, "E10.243.2", {"start": v(28.94, 39.84) * mm, "end": v(32.31, 40.37) * mm});
            skLineSegment(sketch, "E10.244.0", {"start": v(29.38, 42.48) * mm, "end": v(28, 40.5) * mm});
            skLineSegment(sketch, "E10.244.1", {"start": v(31.36, 41.11) * mm, "end": v(29.38, 42.48) * mm});
            skLineSegment(sketch, "E10.244.2", {"start": v(28, 40.5) * mm, "end": v(31.36, 41.11) * mm});
            skLineSegment(sketch, "E10.245.0", {"start": v(28.38, 43.16) * mm, "end": v(27.06, 41.14) * mm});
            skLineSegment(sketch, "E10.245.1", {"start": v(30.4, 41.83) * mm, "end": v(28.38, 43.16) * mm});
            skLineSegment(sketch, "E10.245.2", {"start": v(27.06, 41.14) * mm, "end": v(30.4, 41.83) * mm});
            skLineSegment(sketch, "E10.246.0", {"start": v(27.37, 43.8) * mm, "end": v(26.1, 41.76) * mm});
            skLineSegment(sketch, "E10.246.1", {"start": v(29.42, 42.53) * mm, "end": v(27.37, 43.8) * mm});
            skLineSegment(sketch, "E10.246.2", {"start": v(26.1, 41.76) * mm, "end": v(29.42, 42.53) * mm});
            skLineSegment(sketch, "E10.247.0", {"start": v(26.35, 44.43) * mm, "end": v(25.11, 42.35) * mm});
            skLineSegment(sketch, "E10.247.1", {"start": v(28.42, 43.2) * mm, "end": v(26.35, 44.43) * mm});
            skLineSegment(sketch, "E10.247.2", {"start": v(25.11, 42.35) * mm, "end": v(28.42, 43.2) * mm});
            skLineSegment(sketch, "E10.248.0", {"start": v(25.3, 45.03) * mm, "end": v(24.12, 42.93) * mm});
            skLineSegment(sketch, "E10.248.1", {"start": v(27.4, 43.85) * mm, "end": v(25.3, 45.03) * mm});
            skLineSegment(sketch, "E10.248.2", {"start": v(24.12, 42.93) * mm, "end": v(27.4, 43.85) * mm});
            skLineSegment(sketch, "E10.249.0", {"start": v(24.25, 45.6) * mm, "end": v(23.12, 43.48) * mm});
            skLineSegment(sketch, "E10.249.1", {"start": v(26.38, 44.47) * mm, "end": v(24.25, 45.6) * mm});
            skLineSegment(sketch, "E10.249.2", {"start": v(23.12, 43.48) * mm, "end": v(26.38, 44.47) * mm});
            skLineSegment(sketch, "E10.250.0", {"start": v(23.18, 46.16) * mm, "end": v(22.1, 44) * mm});
            skLineSegment(sketch, "E10.250.1", {"start": v(25.34, 45.08) * mm, "end": v(23.18, 46.16) * mm});
            skLineSegment(sketch, "E10.250.2", {"start": v(22.1, 44) * mm, "end": v(25.34, 45.08) * mm});
            skLineSegment(sketch, "E10.251.0", {"start": v(22.1, 46.69) * mm, "end": v(21.07, 44.5) * mm});
            skLineSegment(sketch, "E10.251.1", {"start": v(24.28, 45.65) * mm, "end": v(22.1, 46.69) * mm});
            skLineSegment(sketch, "E10.251.2", {"start": v(21.07, 44.5) * mm, "end": v(24.28, 45.65) * mm});
            skLineSegment(sketch, "E10.252.0", {"start": v(21, 47.19) * mm, "end": v(20.03, 44.98) * mm});
            skLineSegment(sketch, "E10.252.1", {"start": v(23.21, 46.2) * mm, "end": v(21, 47.19) * mm});
            skLineSegment(sketch, "E10.252.2", {"start": v(20.03, 44.98) * mm, "end": v(23.21, 46.2) * mm});
            skLineSegment(sketch, "E10.253.0", {"start": v(19.9, 47.66) * mm, "end": v(18.98, 45.44) * mm});
            skLineSegment(sketch, "E10.253.1", {"start": v(22.13, 46.73) * mm, "end": v(19.9, 47.66) * mm});
            skLineSegment(sketch, "E10.253.2", {"start": v(18.98, 45.44) * mm, "end": v(22.13, 46.73) * mm});
            skLineSegment(sketch, "E10.254.0", {"start": v(18.8, 48.11) * mm, "end": v(17.91, 45.87) * mm});
            skLineSegment(sketch, "E10.254.1", {"start": v(21.04, 47.24) * mm, "end": v(18.8, 48.11) * mm});
            skLineSegment(sketch, "E10.254.2", {"start": v(17.91, 45.87) * mm, "end": v(21.04, 47.24) * mm});
            skLineSegment(sketch, "E10.255.0", {"start": v(17.67, 48.54) * mm, "end": v(16.84, 46.27) * mm});
            skLineSegment(sketch, "E10.255.1", {"start": v(19.93, 47.71) * mm, "end": v(17.67, 48.54) * mm});
            skLineSegment(sketch, "E10.255.2", {"start": v(16.84, 46.27) * mm, "end": v(19.93, 47.71) * mm});
            skLineSegment(sketch, "E10.256.0", {"start": v(16.53, 48.94) * mm, "end": v(15.76, 46.65) * mm});
            skLineSegment(sketch, "E10.256.1", {"start": v(18.82, 48.16) * mm, "end": v(16.53, 48.94) * mm});
            skLineSegment(sketch, "E10.256.2", {"start": v(15.76, 46.65) * mm, "end": v(18.82, 48.16) * mm});
            skLineSegment(sketch, "E10.257.0", {"start": v(15.39, 49.3) * mm, "end": v(14.67, 47) * mm});
            skLineSegment(sketch, "E10.257.1", {"start": v(17.7, 48.59) * mm, "end": v(15.39, 49.3) * mm});
            skLineSegment(sketch, "E10.257.2", {"start": v(14.67, 47) * mm, "end": v(17.7, 48.59) * mm});
            skLineSegment(sketch, "E10.258.0", {"start": v(14.24, 49.65) * mm, "end": v(13.57, 47.33) * mm});
            skLineSegment(sketch, "E10.258.1", {"start": v(16.56, 48.99) * mm, "end": v(14.24, 49.65) * mm});
            skLineSegment(sketch, "E10.258.2", {"start": v(13.57, 47.33) * mm, "end": v(16.56, 48.99) * mm});
            skLineSegment(sketch, "E10.259.0", {"start": v(13.08, 49.97) * mm, "end": v(12.47, 47.64) * mm});
            skLineSegment(sketch, "E10.259.1", {"start": v(15.41, 49.36) * mm, "end": v(13.08, 49.97) * mm});
            skLineSegment(sketch, "E10.259.2", {"start": v(12.47, 47.64) * mm, "end": v(15.41, 49.36) * mm});
            skLineSegment(sketch, "E10.260.0", {"start": v(11.91, 50.26) * mm, "end": v(11.36, 47.91) * mm});
            skLineSegment(sketch, "E10.260.1", {"start": v(14.26, 49.7) * mm, "end": v(11.91, 50.26) * mm});
            skLineSegment(sketch, "E10.260.2", {"start": v(11.36, 47.91) * mm, "end": v(14.26, 49.7) * mm});
            skLineSegment(sketch, "E10.261.0", {"start": v(10.74, 50.52) * mm, "end": v(10.24, 48.16) * mm});
            skLineSegment(sketch, "E10.261.1", {"start": v(13.1, 50.02) * mm, "end": v(10.74, 50.52) * mm});
            skLineSegment(sketch, "E10.261.2", {"start": v(10.24, 48.16) * mm, "end": v(13.1, 50.02) * mm});
            skLineSegment(sketch, "E10.262.0", {"start": v(9.56, 50.76) * mm, "end": v(9.11, 48.39) * mm});
            skLineSegment(sketch, "E10.262.1", {"start": v(11.93, 50.31) * mm, "end": v(9.56, 50.76) * mm});
            skLineSegment(sketch, "E10.262.2", {"start": v(9.11, 48.39) * mm, "end": v(11.93, 50.31) * mm});
            skLineSegment(sketch, "E10.263.0", {"start": v(8.38, 50.97) * mm, "end": v(7.99, 48.59) * mm});
            skLineSegment(sketch, "E10.263.1", {"start": v(10.76, 50.58) * mm, "end": v(8.38, 50.97) * mm});
            skLineSegment(sketch, "E10.263.2", {"start": v(7.99, 48.59) * mm, "end": v(10.76, 50.58) * mm});
            skLineSegment(sketch, "E10.264.0", {"start": v(7.19, 51.15) * mm, "end": v(6.85, 48.76) * mm});
            skLineSegment(sketch, "E10.264.1", {"start": v(9.58, 50.81) * mm, "end": v(7.19, 51.15) * mm});
            skLineSegment(sketch, "E10.264.2", {"start": v(6.85, 48.76) * mm, "end": v(9.58, 50.81) * mm});
            skLineSegment(sketch, "E10.265.0", {"start": v(6, 51.3) * mm, "end": v(5.72, 48.9) * mm});
            skLineSegment(sketch, "E10.265.1", {"start": v(8.4, 51.02) * mm, "end": v(6, 51.3) * mm});
            skLineSegment(sketch, "E10.265.2", {"start": v(5.72, 48.9) * mm, "end": v(8.4, 51.02) * mm});
            skLineSegment(sketch, "E10.266.0", {"start": v(4.8, 51.43) * mm, "end": v(4.58, 49.03) * mm});
            skLineSegment(sketch, "E10.266.1", {"start": v(7.2, 51.2) * mm, "end": v(4.8, 51.43) * mm});
            skLineSegment(sketch, "E10.266.2", {"start": v(4.58, 49.03) * mm, "end": v(7.2, 51.2) * mm});
            skLineSegment(sketch, "E10.267.0", {"start": v(3.6, 51.53) * mm, "end": v(3.43, 49.12) * mm});
            skLineSegment(sketch, "E10.267.1", {"start": v(6, 51.36) * mm, "end": v(3.6, 51.53) * mm});
            skLineSegment(sketch, "E10.267.2", {"start": v(3.43, 49.12) * mm, "end": v(6, 51.36) * mm});
            skLineSegment(sketch, "E10.268.0", {"start": v(2.4, 51.6) * mm, "end": v(2.3, 49.19) * mm});
            skLineSegment(sketch, "E10.268.1", {"start": v(4.81, 51.49) * mm, "end": v(2.4, 51.6) * mm});
            skLineSegment(sketch, "E10.268.2", {"start": v(2.3, 49.19) * mm, "end": v(4.81, 51.49) * mm});
            skLineSegment(sketch, "E10.269.0", {"start": v(1.2, 51.64) * mm, "end": v(1.15, 49.23) * mm});
            skLineSegment(sketch, "E10.269.1", {"start": v(3.61, 51.58) * mm, "end": v(1.2, 51.64) * mm});
            skLineSegment(sketch, "E10.269.2", {"start": v(1.15, 49.23) * mm, "end": v(3.61, 51.58) * mm});
            skPoint(sketch, "E10.center", {"position": v(0, 0) * mm});
            skSolve(sketch);
        }
        {
            var Q0;
            Q0 = qSketchRegion(id + "F6", true);
            extrude(context, id + "F7", {"entities" : qUnion([Q0]), "operationType" : NewBodyOperationType.REMOVE, "depth" : 9.52 * mm, "hasSecondDirection" : true, "secondDirectionOppositeDirection" : false, "secondDirectionDepth" : 3.17 * mm});
        }
        {
            var Q0;
            {var subQ0=sQuery(id+"F2.wireOp",EDGE,"E5");var subQ1=sQuery(id+"F2.wireOp",EDGE,"E1");Q0=makeQuery(id+"F3bmpaekcYNjjFW_1.boolean.opBoolean","MERGE",FACE,{"derivedFrom":[makeQuery(id+"F1.opExtrude","CAP_FACE",FACE,{"disambiguationData":[OSD([sQuery(id+"F0.wireOp",EDGE,"E0")])],"isStart":false}),makeQuery(id+"F3bmpaekcYNjjFW_1.opExtrude","CAP_FACE",FACE,{"disambiguationData":[OSD([subQ1,sQuery(id+"F2.wireOp",EDGE,"E4.6.0"),sQuery(id+"F2.wireOp",EDGE,"E4.6.1"),subQ0])],"isStart":true}),makeQuery(id+"F3bmpaekcYNjjFW_1.opExtrude","CAP_FACE",FACE,{"disambiguationData":[OSD([subQ1,sQuery(id+"F2.wireOp",EDGE,"E4.7.0"),sQuery(id+"F2.wireOp",EDGE,"E4.7.1"),subQ0])],"isStart":true}),makeQuery(id+"F3bmpaekcYNjjFW_1.opExtrude","CAP_FACE",FACE,{"disambiguationData":[OSD([subQ1,sQuery(id+"F2.wireOp",EDGE,"E2"),sQuery(id+"F2.wireOp",EDGE,"E3"),subQ0])],"isStart":true}),makeQuery(id+"F3bmpaekcYNjjFW_1.opExtrude","CAP_FACE",FACE,{"disambiguationData":[OSD([subQ1,sQuery(id+"F2.wireOp",EDGE,"E4.1.0"),sQuery(id+"F2.wireOp",EDGE,"E4.1.1"),subQ0])],"isStart":true}),makeQuery(id+"F3bmpaekcYNjjFW_1.opExtrude","CAP_FACE",FACE,{"disambiguationData":[OSD([subQ1,sQuery(id+"F2.wireOp",EDGE,"E4.2.0"),sQuery(id+"F2.wireOp",EDGE,"E4.2.1"),subQ0])],"isStart":true}),makeQuery(id+"F3bmpaekcYNjjFW_1.opExtrude","CAP_FACE",FACE,{"disambiguationData":[OSD([subQ1,sQuery(id+"F2.wireOp",EDGE,"E4.3.0"),sQuery(id+"F2.wireOp",EDGE,"E4.3.1"),subQ0])],"isStart":true}),makeQuery(id+"F3bmpaekcYNjjFW_1.opExtrude","CAP_FACE",FACE,{"disambiguationData":[OSD([subQ1,sQuery(id+"F2.wireOp",EDGE,"E4.4.0"),sQuery(id+"F2.wireOp",EDGE,"E4.4.1"),subQ0])],"isStart":true}),makeQuery(id+"F3bmpaekcYNjjFW_1.opExtrude","CAP_FACE",FACE,{"disambiguationData":[OSD([subQ1,sQuery(id+"F2.wireOp",EDGE,"E4.5.0"),sQuery(id+"F2.wireOp",EDGE,"E4.5.1"),subQ0])],"isStart":true})]});}
            var sketch = newSketch(context, id + "F8", { "sketchPlane" : qUnion([Q0])});
            skCircle(sketch, "E11", {"center": v(0, 47.62) * mm, "radius": 0.95 * mm});
            skCircle(sketch, "E12.1.0", {"center": v(-3, 47.53) * mm, "radius": 0.95 * mm});
            skCircle(sketch, "E12.2.0", {"center": v(-5.97, 47.25) * mm, "radius": 0.95 * mm});
            skCircle(sketch, "E12.3.0", {"center": v(-8.92, 46.78) * mm, "radius": 0.95 * mm});
            skCircle(sketch, "E12.4.0", {"center": v(-11.84, 46.13) * mm, "radius": 0.95 * mm});
            skCircle(sketch, "E12.5.0", {"center": v(-14.72, 45.3) * mm, "radius": 0.95 * mm});
            skCircle(sketch, "E12.6.0", {"center": v(-17.53, 44.28) * mm, "radius": 0.95 * mm});
            skCircle(sketch, "E12.7.0", {"center": v(-20.28, 43.1) * mm, "radius": 0.95 * mm});
            skCircle(sketch, "E12.8.0", {"center": v(-22.94, 41.73) * mm, "radius": 0.95 * mm});
            skCircle(sketch, "E12.9.0", {"center": v(-25.52, 40.21) * mm, "radius": 0.95 * mm});
            skCircle(sketch, "E12.10.0", {"center": v(-28, 38.53) * mm, "radius": 0.95 * mm});
            skCircle(sketch, "E12.11.0", {"center": v(-30.36, 36.7) * mm, "radius": 0.95 * mm});
            skCircle(sketch, "E12.12.0", {"center": v(-32.6, 34.72) * mm, "radius": 0.95 * mm});
            skCircle(sketch, "E12.13.0", {"center": v(-34.72, 32.6) * mm, "radius": 0.95 * mm});
            skCircle(sketch, "E12.14.0", {"center": v(-36.7, 30.36) * mm, "radius": 0.95 * mm});
            skCircle(sketch, "E12.15.0", {"center": v(-38.53, 28) * mm, "radius": 0.95 * mm});
            skCircle(sketch, "E12.16.0", {"center": v(-40.21, 25.52) * mm, "radius": 0.95 * mm});
            skCircle(sketch, "E12.17.0", {"center": v(-41.73, 22.94) * mm, "radius": 0.95 * mm});
            skCircle(sketch, "E12.18.0", {"center": v(-43.1, 20.28) * mm, "radius": 0.95 * mm});
            skCircle(sketch, "E12.19.0", {"center": v(-44.28, 17.53) * mm, "radius": 0.95 * mm});
            skCircle(sketch, "E12.20.0", {"center": v(-45.3, 14.72) * mm, "radius": 0.95 * mm});
            skCircle(sketch, "E12.21.0", {"center": v(-46.13, 11.84) * mm, "radius": 0.95 * mm});
            skCircle(sketch, "E12.22.0", {"center": v(-46.78, 8.92) * mm, "radius": 0.95 * mm});
            skCircle(sketch, "E12.23.0", {"center": v(-47.25, 5.97) * mm, "radius": 0.95 * mm});
            skCircle(sketch, "E12.24.0", {"center": v(-47.53, 3) * mm, "radius": 0.95 * mm});
            skCircle(sketch, "E12.25.0", {"center": v(-47.62, 0) * mm, "radius": 0.95 * mm});
            skCircle(sketch, "E12.26.0", {"center": v(-47.53, -3) * mm, "radius": 0.95 * mm});
            skCircle(sketch, "E12.27.0", {"center": v(-47.25, -5.97) * mm, "radius": 0.95 * mm});
            skCircle(sketch, "E12.28.0", {"center": v(-46.78, -8.92) * mm, "radius": 0.95 * mm});
            skCircle(sketch, "E12.29.0", {"center": v(-46.13, -11.84) * mm, "radius": 0.95 * mm});
            skCircle(sketch, "E12.30.0", {"center": v(-45.3, -14.72) * mm, "radius": 0.95 * mm});
            skCircle(sketch, "E12.31.0", {"center": v(-44.28, -17.53) * mm, "radius": 0.95 * mm});
            skCircle(sketch, "E12.32.0", {"center": v(-43.1, -20.28) * mm, "radius": 0.95 * mm});
            skCircle(sketch, "E12.33.0", {"center": v(-41.73, -22.94) * mm, "radius": 0.95 * mm});
            skCircle(sketch, "E12.34.0", {"center": v(-40.21, -25.52) * mm, "radius": 0.95 * mm});
            skCircle(sketch, "E12.35.0", {"center": v(-38.53, -28) * mm, "radius": 0.95 * mm});
            skCircle(sketch, "E12.36.0", {"center": v(-36.7, -30.36) * mm, "radius": 0.95 * mm});
            skCircle(sketch, "E12.37.0", {"center": v(-34.72, -32.6) * mm, "radius": 0.95 * mm});
            skCircle(sketch, "E12.38.0", {"center": v(-32.6, -34.72) * mm, "radius": 0.95 * mm});
            skCircle(sketch, "E12.39.0", {"center": v(-30.36, -36.7) * mm, "radius": 0.95 * mm});
            skCircle(sketch, "E12.40.0", {"center": v(-28, -38.53) * mm, "radius": 0.95 * mm});
            skCircle(sketch, "E12.41.0", {"center": v(-25.52, -40.21) * mm, "radius": 0.95 * mm});
            skCircle(sketch, "E12.42.0", {"center": v(-22.94, -41.73) * mm, "radius": 0.95 * mm});
            skCircle(sketch, "E12.43.0", {"center": v(-20.28, -43.1) * mm, "radius": 0.95 * mm});
            skCircle(sketch, "E12.44.0", {"center": v(-17.53, -44.28) * mm, "radius": 0.95 * mm});
            skCircle(sketch, "E12.45.0", {"center": v(-14.72, -45.3) * mm, "radius": 0.95 * mm});
            skCircle(sketch, "E12.46.0", {"center": v(-11.84, -46.13) * mm, "radius": 0.95 * mm});
            skCircle(sketch, "E12.47.0", {"center": v(-8.92, -46.78) * mm, "radius": 0.95 * mm});
            skCircle(sketch, "E12.48.0", {"center": v(-5.97, -47.25) * mm, "radius": 0.95 * mm});
            skCircle(sketch, "E12.49.0", {"center": v(-3, -47.53) * mm, "radius": 0.95 * mm});
            skCircle(sketch, "E12.50.0", {"center": v(0, -47.62) * mm, "radius": 0.95 * mm});
            skCircle(sketch, "E12.51.0", {"center": v(3, -47.53) * mm, "radius": 0.95 * mm});
            skCircle(sketch, "E12.52.0", {"center": v(5.97, -47.25) * mm, "radius": 0.95 * mm});
            skCircle(sketch, "E12.53.0", {"center": v(8.92, -46.78) * mm, "radius": 0.95 * mm});
            skCircle(sketch, "E12.54.0", {"center": v(11.84, -46.13) * mm, "radius": 0.95 * mm});
            skCircle(sketch, "E12.55.0", {"center": v(14.72, -45.3) * mm, "radius": 0.95 * mm});
            skCircle(sketch, "E12.56.0", {"center": v(17.53, -44.28) * mm, "radius": 0.95 * mm});
            skCircle(sketch, "E12.57.0", {"center": v(20.28, -43.1) * mm, "radius": 0.95 * mm});
            skCircle(sketch, "E12.58.0", {"center": v(22.94, -41.73) * mm, "radius": 0.95 * mm});
            skCircle(sketch, "E12.59.0", {"center": v(25.52, -40.21) * mm, "radius": 0.95 * mm});
            skCircle(sketch, "E12.60.0", {"center": v(28, -38.53) * mm, "radius": 0.95 * mm});
            skCircle(sketch, "E12.61.0", {"center": v(30.36, -36.7) * mm, "radius": 0.95 * mm});
            skCircle(sketch, "E12.62.0", {"center": v(32.6, -34.72) * mm, "radius": 0.95 * mm});
            skCircle(sketch, "E12.63.0", {"center": v(34.72, -32.6) * mm, "radius": 0.95 * mm});
            skCircle(sketch, "E12.64.0", {"center": v(36.7, -30.36) * mm, "radius": 0.95 * mm});
            skCircle(sketch, "E12.65.0", {"center": v(38.53, -28) * mm, "radius": 0.95 * mm});
            skCircle(sketch, "E12.66.0", {"center": v(40.21, -25.52) * mm, "radius": 0.95 * mm});
            skCircle(sketch, "E12.67.0", {"center": v(41.73, -22.94) * mm, "radius": 0.95 * mm});
            skCircle(sketch, "E12.68.0", {"center": v(43.1, -20.28) * mm, "radius": 0.95 * mm});
            skCircle(sketch, "E12.69.0", {"center": v(44.28, -17.53) * mm, "radius": 0.95 * mm});
            skCircle(sketch, "E12.70.0", {"center": v(45.3, -14.72) * mm, "radius": 0.95 * mm});
            skCircle(sketch, "E12.71.0", {"center": v(46.13, -11.84) * mm, "radius": 0.95 * mm});
            skCircle(sketch, "E12.72.0", {"center": v(46.78, -8.92) * mm, "radius": 0.95 * mm});
            skCircle(sketch, "E12.73.0", {"center": v(47.25, -5.97) * mm, "radius": 0.95 * mm});
            skCircle(sketch, "E12.74.0", {"center": v(47.53, -3) * mm, "radius": 0.95 * mm});
            skCircle(sketch, "E12.75.0", {"center": v(47.62, 0) * mm, "radius": 0.95 * mm});
            skCircle(sketch, "E12.76.0", {"center": v(47.53, 3) * mm, "radius": 0.95 * mm});
            skCircle(sketch, "E12.77.0", {"center": v(47.25, 5.97) * mm, "radius": 0.95 * mm});
            skCircle(sketch, "E12.78.0", {"center": v(46.78, 8.92) * mm, "radius": 0.95 * mm});
            skCircle(sketch, "E12.79.0", {"center": v(46.13, 11.84) * mm, "radius": 0.95 * mm});
            skCircle(sketch, "E12.80.0", {"center": v(45.3, 14.72) * mm, "radius": 0.95 * mm});
            skCircle(sketch, "E12.81.0", {"center": v(44.28, 17.53) * mm, "radius": 0.95 * mm});
            skCircle(sketch, "E12.82.0", {"center": v(43.1, 20.28) * mm, "radius": 0.95 * mm});
            skCircle(sketch, "E12.83.0", {"center": v(41.73, 22.94) * mm, "radius": 0.95 * mm});
            skCircle(sketch, "E12.84.0", {"center": v(40.21, 25.52) * mm, "radius": 0.95 * mm});
            skCircle(sketch, "E12.85.0", {"center": v(38.53, 28) * mm, "radius": 0.95 * mm});
            skCircle(sketch, "E12.86.0", {"center": v(36.7, 30.36) * mm, "radius": 0.95 * mm});
            skCircle(sketch, "E12.87.0", {"center": v(34.72, 32.6) * mm, "radius": 0.95 * mm});
            skCircle(sketch, "E12.88.0", {"center": v(32.6, 34.72) * mm, "radius": 0.95 * mm});
            skCircle(sketch, "E12.89.0", {"center": v(30.36, 36.7) * mm, "radius": 0.95 * mm});
            skCircle(sketch, "E12.90.0", {"center": v(28, 38.53) * mm, "radius": 0.95 * mm});
            skCircle(sketch, "E12.91.0", {"center": v(25.52, 40.21) * mm, "radius": 0.95 * mm});
            skCircle(sketch, "E12.92.0", {"center": v(22.94, 41.73) * mm, "radius": 0.95 * mm});
            skCircle(sketch, "E12.93.0", {"center": v(20.28, 43.1) * mm, "radius": 0.95 * mm});
            skCircle(sketch, "E12.94.0", {"center": v(17.53, 44.28) * mm, "radius": 0.95 * mm});
            skCircle(sketch, "E12.95.0", {"center": v(14.72, 45.3) * mm, "radius": 0.95 * mm});
            skCircle(sketch, "E12.96.0", {"center": v(11.84, 46.13) * mm, "radius": 0.95 * mm});
            skCircle(sketch, "E12.97.0", {"center": v(8.92, 46.78) * mm, "radius": 0.95 * mm});
            skCircle(sketch, "E12.98.0", {"center": v(5.97, 47.25) * mm, "radius": 0.95 * mm});
            skCircle(sketch, "E12.99.0", {"center": v(3, 47.53) * mm, "radius": 0.95 * mm});
            skPoint(sketch, "E12.center", {"position": v(0, 0) * mm});
            skSolve(sketch);
        }
        {
            var Q0;
            Q0 = qSketchRegion(id + "F8", true);
            extrude(context, id + "F9", {"entities" : qUnion([Q0]), "operationType" : NewBodyOperationType.REMOVE, "oppositeDirection" : true, "depth" : 1.27 * mm});
        }
        {
            var Q0;
            Q0=makeQuery(id+"F3.boolean.opBoolean","COPY",FACE,{"derivedFrom":makeQuery(id+"F3.opExtrude","CAP_FACE",FACE,{"disambiguationData":[OSD([sQuery(id+"F2.wireOp",EDGE,"E1")])],"isStart":false})});
            var sketch = newSketch(context, id + "F10", { "sketchPlane" : qUnion([Q0])});
            skCircle(sketch, "E13", {"center": v(0, 0) * mm, "radius": 41.28 * mm});
            skSolve(sketch);
        }
        {
            var Q0;
            Q0 = qSketchRegion(id + "F10", true);
            extrude(context, id + "F11", {"entities" : qUnion([Q0]), "operationType" : NewBodyOperationType.REMOVE, "depth" : 3.17 * mm});
        }
        {
            var Q0;
            Q0=makeQuery(id+"F11.boolean.opBoolean","MERGE",FACE,{"derivedFrom":[makeQuery(id+"F3.boolean.opBoolean","COPY",FACE,{"derivedFrom":makeQuery(id+"F3.opExtrude","CAP_FACE",FACE,{"disambiguationData":[OSD([sQuery(id+"F2.wireOp",EDGE,"E1")])],"isStart":false})}),makeQuery(id+"F11.opExtrude","CAP_FACE",FACE,{"disambiguationData":[OSD([sQuery(id+"F10.wireOp",EDGE,"E13")])],"isStart":true})]});
            var sketch = newSketch(context, id + "F12", { "sketchPlane" : qUnion([Q0])});
            skCircle(sketch, "E14", {"center": v(0, 0) * mm, "radius": 6.35 * mm});
            skCircle(sketch, "E15", {"center": v(0, 0) * mm, "radius": 9.53 * mm});
            skSolve(sketch);
        }
        {
            var Q0;
            Q0=makeQuery(id+"F12.imprint","IMPRINT",FACE,{"disambiguationData":[TD([[makeQuery(id+"F12.imprint","IMPRINT",EDGE,{"derivedFrom":sQuery(id+"F12.wireOp",EDGE,"E14")}),-1.0]])]});
            var Q1;
            Q1=makeQuery(id+"F12.imprint","IMPRINT",FACE,{"disambiguationData":[TD([[makeQuery(id+"F12.imprint","IMPRINT",EDGE,{"derivedFrom":sQuery(id+"F12.wireOp",EDGE,"E14")}),1.0]])]});
            extrude(context, id + "F13", {"entities" : qUnion([Q0, Q1]), "operationType" : NewBodyOperationType.ADD, "depth" : 6.35 * mm});
        }
        {
            var Q0;
            Q0 = qSketchRegion(id + "F12", true);
            extrude(context, id + "F14", {"entities" : qUnion([Q0]), "operationType" : NewBodyOperationType.REMOVE, "depth" : 3.17 * mm});
        }
        {
            var Q0;
            Q0=makeQuery(id+"F3.boolean.opBoolean","COPY",EDGE,{"derivedFrom":makeQuery(id+"F3.opExtrude","CAP_EDGE",EDGE,{"disambiguationData":[OSD([sQuery(id+"F2.wireOp",EDGE,"E1")])],"isStart":true})});
            var Q1;
            Q1=makeQuery(id+"F5.boolean.opBoolean","INTERSECT",EDGE,{"derivedFrom":[makeQuery(id+"F1.opExtrude","CAP_FACE",FACE,{"disambiguationData":[OSD([sQuery(id+"F0.wireOp",EDGE,"E0")])],"isStart":true}),makeQuery(id+"F5.opExtrude","SWEPT_FACE",FACE,{"disambiguationData":[OSD([sQuery(id+"F4.wireOp",EDGE,"E6")])]})]});
            var Q2;
            {var subQ0=sQuery(id+"F0.wireOp",EDGE,"E0");Q2=makeQuery(id+"FsqNVuNjpUWVb5P_1.boolean.opBoolean","SPLIT",EDGE,{"disambiguationData":[TD([makeQuery(id+"FsqNVuNjpUWVb5P_1.opExtrude","SWEPT_FACE",FACE,{"disambiguationData":[OSD([sQuery(id+"FS9hs2E55j3BQ7e_1.wireOp",EDGE,"879fb005-e0db-42de-a008-25bc68587a08.left")])]})])],"derivedFrom":makeQuery(id+"F1.opExtrude","CAP_EDGE",EDGE,{"disambiguationData":[OSD([subQ0])],"isStart":false})});}
            var Q3;
            {var subQ0=sQuery(id+"F0.wireOp",EDGE,"E0");Q3=makeQuery(id+"FsqNVuNjpUWVb5P_1.boolean.opBoolean","SPLIT",EDGE,{"disambiguationData":[TD([makeQuery(id+"FsqNVuNjpUWVb5P_1.opExtrude","SWEPT_FACE",FACE,{"disambiguationData":[OSD([sQuery(id+"FS9hs2E55j3BQ7e_1.wireOp",EDGE,"879fb005-e0db-42de-a008-25bc68587a08.right")])]})])],"derivedFrom":makeQuery(id+"F1.opExtrude","CAP_EDGE",EDGE,{"disambiguationData":[OSD([subQ0])],"isStart":false})});}
            var Q4;
            {var subQ0=sQuery(id+"F0.wireOp",EDGE,"E0");Q4=makeQuery(id+"FsqNVuNjpUWVb5P_1.boolean.opBoolean","SPLIT",EDGE,{"disambiguationData":[TD([makeQuery(id+"FsqNVuNjpUWVb5P_1.opExtrude","SWEPT_FACE",FACE,{"disambiguationData":[OSD([sQuery(id+"FS9hs2E55j3BQ7e_1.wireOp",EDGE,"3561610d-a3e4-4b20-9882-0e1d9f489c4b.right")])]})])],"derivedFrom":makeQuery(id+"F1.opExtrude","CAP_EDGE",EDGE,{"disambiguationData":[OSD([subQ0])],"isStart":false})});}
            var Q5;
            {var subQ0=sQuery(id+"F0.wireOp",EDGE,"E0");Q5=makeQuery(id+"FsqNVuNjpUWVb5P_1.boolean.opBoolean","SPLIT",EDGE,{"disambiguationData":[TD([makeQuery(id+"FsqNVuNjpUWVb5P_1.opExtrude","SWEPT_FACE",FACE,{"disambiguationData":[OSD([sQuery(id+"FS9hs2E55j3BQ7e_1.wireOp",EDGE,"862e82db-a281-4ee4-890f-9746a01467a5.top")])]})])],"derivedFrom":makeQuery(id+"F1.opExtrude","CAP_EDGE",EDGE,{"disambiguationData":[OSD([subQ0])],"isStart":false})});}
            var Q6;
            Q6=makeQuery(id+"F1.opExtrude","CAP_EDGE",EDGE,{"disambiguationData":[OSD([sQuery(id+"F0.wireOp",EDGE,"E0")])],"isStart":true});
            var Q7;
            Q7=makeQuery(id+"F11.boolean.opBoolean","COPY",FACE,{"derivedFrom":makeQuery(id+"F11.opExtrude","SWEPT_FACE",FACE,{"disambiguationData":[OSD([sQuery(id+"F10.wireOp",EDGE,"E13")])]})});
            var Q8;
            Q8=makeQuery(id+"F11.boolean.opBoolean","INTERSECT",EDGE,{"derivedFrom":[makeQuery(id+"F3.boolean.opBoolean","COPY",FACE,{"derivedFrom":makeQuery(id+"F3.opExtrude","SWEPT_FACE",FACE,{"disambiguationData":[OSD([sQuery(id+"F2.wireOp",EDGE,"E1")])]})}),makeQuery(id+"F11.opExtrude","CAP_FACE",FACE,{"disambiguationData":[OSD([sQuery(id+"F10.wireOp",EDGE,"E13")])],"isStart":false})]});
            var Q9;
            Q9=makeQuery(id+"F14.boolean.opBoolean","COPY",FACE,{"derivedFrom":makeQuery(id+"F14.opExtrude","SWEPT_FACE",FACE,{"disambiguationData":[OSD([sQuery(id+"F12.wireOp",EDGE,"E14")])]})});
            var Q10;
            Q10=makeQuery(id+"F13.opExtrude","SWEPT_FACE",FACE,{"disambiguationData":[OSD([sQuery(id+"F12.wireOp",EDGE,"E15")])]});
            var Q11;
            Q11=makeQuery(id+"F13.opExtrude","CAP_EDGE",EDGE,{"disambiguationData":[OSD([sQuery(id+"F4.wireOp",EDGE,"E6")])],"isStart":false});
            fillet(context, id + "F15", {"entities" : qUnion([Q0, Q1, Q2, Q3, Q4, Q5, Q6, Q7, Q8, Q9, Q10, Q11]), "radius" : 1.59 * mm, "tangentPropagation" : true, "allowEdgeOverflow" : false});
        }
        {
            var Q0;
            Q0=makeQuery(id+"F1.opExtrude","CAP_FACE",FACE,{"disambiguationData":[OSD([sQuery(id+"F0.wireOp",EDGE,"E0")])],"isStart":false});
            var sketch = newSketch(context, id + "F16", { "sketchPlane" : qUnion([Q0])});
            skEllipse(sketch, "E16", {"center": v(0, 39.69) * mm, "majorRadius": 1.59 * mm, "minorRadius": 1.59 * mm, "majorAxis": v(0, 1)});
            skLineSegment(sketch, "E17.bottom", {"start": v(-1.59, 39.66) * mm, "end": v(1.59, 39.66) * mm});
            skLineSegment(sketch, "E17.top", {"start": v(-1.59, 36.54) * mm, "end": v(1.59, 36.54) * mm});
            skLineSegment(sketch, "E17.left", {"start": v(-1.59, 39.66) * mm, "end": v(-1.59, 36.54) * mm});
            skLineSegment(sketch, "E17.right", {"start": v(1.59, 39.66) * mm, "end": v(1.59, 36.54) * mm});
            skPoint(sketch, "E17.middle", {"position": v(0, 38.1) * mm});
            skPoint(sketch, "E17.cornerSnap0", {"position": v(-1.59, 39.69) * mm});
            skSolve(sketch);
        }
        {
            var Q0;
            Q0 = qSketchRegion(id + "F16", true);
            extrude(context, id + "F17", {"entities" : qUnion([Q0]), "operationType" : NewBodyOperationType.REMOVE, "oppositeDirection" : true, "depth" : 4.76 * mm});
        }
    });
